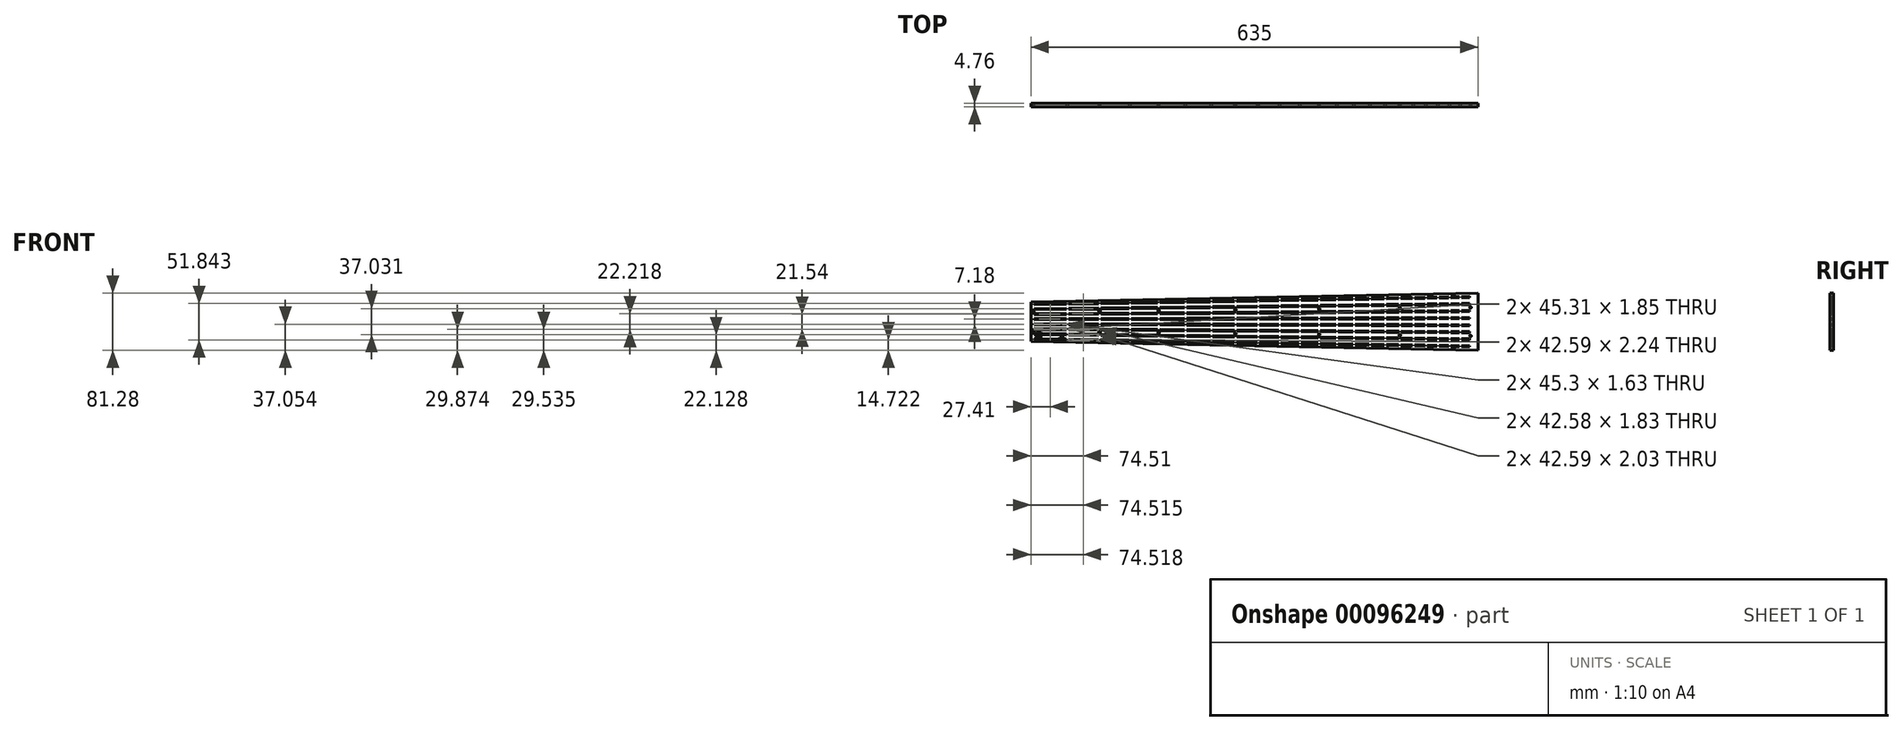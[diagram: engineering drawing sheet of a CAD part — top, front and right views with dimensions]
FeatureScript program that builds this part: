
annotation { "Feature Type Name" : "Feature", "Feature Type Description" : "" }
export const myFeature = defineFeature(function(context is Context, id is Id, definition is map)
    precondition{}
    {
        {
            var Q0;
            Q0=qCreatedBy(makeId("Front.planeOp"),FACE);
            var sketch = newSketch(context, id + "F0", { "sketchPlane" : qUnion([Q0])});
            skLineSegment(sketch, "E0", {"start": v(0, 3.52) * mm, "end": v(648.16, -7.37) * mm, "construction": true});
            skLineSegment(sketch, "E1", {"start": v(0, 4.29) * mm, "end": v(642.9, -6.52) * mm, "construction": true});
            skLineSegment(sketch, "E2", {"start": v(4.76, 3.44) * mm, "end": v(4.77, 4.2) * mm});
            skLineSegment(sketch, "E3", {"start": v(4.77, 4.2) * mm, "end": v(50.06, 3.45) * mm});
            skLineSegment(sketch, "E4", {"start": v(50.06, 3.45) * mm, "end": v(50.05, 2.68) * mm});
            skLineSegment(sketch, "E5", {"start": v(53.23, 2.63) * mm, "end": v(53.24, 3.4) * mm});
            skLineSegment(sketch, "E6", {"start": v(53.24, 3.4) * mm, "end": v(95.8, 2.68) * mm});
            skLineSegment(sketch, "E7", {"start": v(95.8, 2.68) * mm, "end": v(95.8, 1.91) * mm});
            skLineSegment(sketch, "E8", {"start": v(98.97, 1.86) * mm, "end": v(98.98, 2.62) * mm});
            skLineSegment(sketch, "E9", {"start": v(98.98, 2.62) * mm, "end": v(138.98, 1.95) * mm});
            skLineSegment(sketch, "E10", {"start": v(138.98, 1.95) * mm, "end": v(138.97, 1.19) * mm});
            skLineSegment(sketch, "E11", {"start": v(142.14, 1.14) * mm, "end": v(142.16, 1.9) * mm});
            skLineSegment(sketch, "E12", {"start": v(142.16, 1.9) * mm, "end": v(179.73, 1.27) * mm});
            skLineSegment(sketch, "E13", {"start": v(179.73, 1.27) * mm, "end": v(179.72, 0.5) * mm});
            skLineSegment(sketch, "E14", {"start": v(182.89, 0.45) * mm, "end": v(182.9, 1.21) * mm});
            skLineSegment(sketch, "E15", {"start": v(182.9, 1.21) * mm, "end": v(218.2, 0.62) * mm, "construction": true});
            skLineSegment(sketch, "E16", {"start": v(218.2, 0.62) * mm, "end": v(218.19, -0.14) * mm});
            skLineSegment(sketch, "E17", {"start": v(221.36, -0.2) * mm, "end": v(221.38, 0.57) * mm});
            skLineSegment(sketch, "E18", {"start": v(221.38, 0.57) * mm, "end": v(254.5, 0.01) * mm});
            skLineSegment(sketch, "E19", {"start": v(254.5, 0.01) * mm, "end": v(254.5, -0.75) * mm});
            skLineSegment(sketch, "E20", {"start": v(257.67, -0.8) * mm, "end": v(257.68, -0.04) * mm});
            skLineSegment(sketch, "E21", {"start": v(257.68, -0.04) * mm, "end": v(288.78, -0.57) * mm});
            skLineSegment(sketch, "E22", {"start": v(288.78, -0.57) * mm, "end": v(288.76, -1.33) * mm});
            skLineSegment(sketch, "E23", {"start": v(291.94, -1.38) * mm, "end": v(291.95, -0.62) * mm});
            skLineSegment(sketch, "E24", {"start": v(291.95, -0.62) * mm, "end": v(321.12, -1.1) * mm});
            skLineSegment(sketch, "E25", {"start": v(321.12, -1.1) * mm, "end": v(321.1, -1.87) * mm});
            skLineSegment(sketch, "E26", {"start": v(324.28, -1.92) * mm, "end": v(324.3, -1.16) * mm});
            skLineSegment(sketch, "E27", {"start": v(324.3, -1.16) * mm, "end": v(351.65, -1.62) * mm});
            skLineSegment(sketch, "E28", {"start": v(351.65, -1.62) * mm, "end": v(351.64, -2.38) * mm});
            skLineSegment(sketch, "E29", {"start": v(182.9, 1.21) * mm, "end": v(218.2, 0.62) * mm});
            skLineSegment(sketch, "E30", {"start": v(354.81, -2.44) * mm, "end": v(354.83, -1.68) * mm});
            skLineSegment(sketch, "E31", {"start": v(354.83, -1.68) * mm, "end": v(380.47, -2.1) * mm});
            skLineSegment(sketch, "E32", {"start": v(380.47, -2.1) * mm, "end": v(380.45, -2.87) * mm});
            skLineSegment(sketch, "E33", {"start": v(383.63, -2.92) * mm, "end": v(383.64, -2.16) * mm});
            skLineSegment(sketch, "E34", {"start": v(383.64, -2.16) * mm, "end": v(407.67, -2.56) * mm});
            skLineSegment(sketch, "E35", {"start": v(407.67, -2.56) * mm, "end": v(407.65, -3.33) * mm});
            skLineSegment(sketch, "E36", {"start": v(410.83, -3.38) * mm, "end": v(410.84, -2.62) * mm});
            skLineSegment(sketch, "E37", {"start": v(410.84, -2.62) * mm, "end": v(433.34, -3) * mm});
            skLineSegment(sketch, "E38", {"start": v(433.34, -3) * mm, "end": v(433.33, -3.76) * mm});
            skLineSegment(sketch, "E39", {"start": v(436.5, -3.8) * mm, "end": v(436.51, -3.05) * mm});
            skLineSegment(sketch, "E40", {"start": v(436.51, -3.05) * mm, "end": v(457.57, -3.4) * mm});
            skLineSegment(sketch, "E41", {"start": v(457.57, -3.4) * mm, "end": v(457.56, -4.16) * mm});
            skLineSegment(sketch, "E42", {"start": v(460.73, -4.22) * mm, "end": v(460.75, -3.46) * mm});
            skLineSegment(sketch, "E43", {"start": v(460.75, -3.46) * mm, "end": v(480.44, -3.79) * mm});
            skLineSegment(sketch, "E44", {"start": v(480.44, -3.79) * mm, "end": v(480.43, -4.55) * mm});
            skLineSegment(sketch, "E45", {"start": v(483.6, -4.6) * mm, "end": v(483.62, -3.84) * mm});
            skLineSegment(sketch, "E46", {"start": v(483.62, -3.84) * mm, "end": v(502.03, -4.15) * mm});
            skLineSegment(sketch, "E47", {"start": v(502.03, -4.15) * mm, "end": v(502.02, -4.91) * mm});
            skLineSegment(sketch, "E48", {"start": v(505.2, -4.96) * mm, "end": v(505.2, -4.2) * mm});
            skLineSegment(sketch, "E49", {"start": v(505.2, -4.2) * mm, "end": v(522.4, -4.5) * mm});
            skLineSegment(sketch, "E50", {"start": v(522.4, -4.5) * mm, "end": v(522.4, -5.25) * mm});
            skLineSegment(sketch, "E51", {"start": v(525.57, -5.3) * mm, "end": v(525.58, -4.54) * mm});
            skLineSegment(sketch, "E52", {"start": v(525.58, -4.54) * mm, "end": v(541.64, -4.81) * mm});
            skLineSegment(sketch, "E53", {"start": v(541.64, -4.81) * mm, "end": v(541.63, -5.58) * mm});
            skLineSegment(sketch, "E54", {"start": v(544.8, -5.63) * mm, "end": v(544.81, -4.87) * mm});
            skLineSegment(sketch, "E55", {"start": v(544.81, -4.87) * mm, "end": v(559.8, -5.12) * mm});
            skLineSegment(sketch, "E56", {"start": v(559.8, -5.12) * mm, "end": v(559.78, -5.88) * mm});
            skLineSegment(sketch, "E57", {"start": v(562.95, -5.93) * mm, "end": v(562.97, -5.17) * mm});
            skLineSegment(sketch, "E58", {"start": v(562.97, -5.17) * mm, "end": v(576.93, -5.4) * mm});
            skLineSegment(sketch, "E59", {"start": v(576.93, -5.4) * mm, "end": v(576.91, -6.17) * mm});
            skLineSegment(sketch, "E60", {"start": v(580.09, -6.22) * mm, "end": v(580.1, -5.46) * mm});
            skLineSegment(sketch, "E61", {"start": v(580.1, -5.46) * mm, "end": v(593.1, -5.68) * mm});
            skLineSegment(sketch, "E62", {"start": v(593.1, -5.68) * mm, "end": v(593.09, -6.44) * mm});
            skLineSegment(sketch, "E63", {"start": v(596.26, -6.5) * mm, "end": v(596.27, -5.73) * mm});
            skLineSegment(sketch, "E64", {"start": v(596.27, -5.73) * mm, "end": v(608.36, -5.94) * mm});
            skLineSegment(sketch, "E65", {"start": v(608.36, -5.94) * mm, "end": v(608.35, -6.7) * mm});
            skLineSegment(sketch, "E66", {"start": v(611.53, -6.75) * mm, "end": v(611.54, -5.99) * mm});
            skLineSegment(sketch, "E67", {"start": v(611.54, -5.99) * mm, "end": v(622.77, -6.18) * mm});
            skLineSegment(sketch, "E68", {"start": v(622.77, -6.18) * mm, "end": v(622.76, -6.94) * mm});
            skLineSegment(sketch, "E69.MirrorCS", {"start": v(182.89, 0.45) * mm, "end": v(182.88, -0.31) * mm});
            skLineSegment(sketch, "E70.MirrorCS", {"start": v(608.34, -7.46) * mm, "end": v(608.35, -6.7) * mm});
            skLineSegment(sketch, "E71.MirrorCS", {"start": v(221.36, -0.2) * mm, "end": v(221.35, -0.96) * mm});
            skLineSegment(sketch, "E72.MirrorCS", {"start": v(559.77, -6.64) * mm, "end": v(559.78, -5.88) * mm});
            skLineSegment(sketch, "E73.MirrorCS", {"start": v(218.18, -0.9) * mm, "end": v(218.19, -0.14) * mm});
            skLineSegment(sketch, "E74.MirrorCS", {"start": v(291.94, -1.38) * mm, "end": v(291.92, -2.14) * mm});
            skLineSegment(sketch, "E75.MirrorCS", {"start": v(95.78, 1.15) * mm, "end": v(95.8, 1.91) * mm});
            skLineSegment(sketch, "E76.MirrorCS", {"start": v(50.04, 1.92) * mm, "end": v(50.05, 2.68) * mm});
            skLineSegment(sketch, "E77.MirrorCS", {"start": v(611.53, -6.75) * mm, "end": v(611.51, -7.51) * mm});
            skLineSegment(sketch, "E78.MirrorCS", {"start": v(596.26, -6.5) * mm, "end": v(596.25, -7.26) * mm});
            skLineSegment(sketch, "E79.MirrorCS", {"start": v(324.28, -1.92) * mm, "end": v(324.27, -2.69) * mm});
            skLineSegment(sketch, "E80.MirrorCS", {"start": v(580.09, -6.22) * mm, "end": v(580.08, -6.98) * mm});
            skLineSegment(sketch, "E81.MirrorCS", {"start": v(480.42, -5.3) * mm, "end": v(480.43, -4.55) * mm});
            skLineSegment(sketch, "E82.MirrorCS", {"start": v(407.64, -4.09) * mm, "end": v(407.65, -3.33) * mm});
            skLineSegment(sketch, "E83.MirrorCS", {"start": v(593.07, -7.2) * mm, "end": v(593.09, -6.44) * mm});
            skLineSegment(sketch, "E84.MirrorCS", {"start": v(483.6, -4.6) * mm, "end": v(483.6, -5.36) * mm});
            skLineSegment(sketch, "E85.MirrorCS", {"start": v(580.08, -6.98) * mm, "end": v(593.07, -7.2) * mm});
            skLineSegment(sketch, "E86.MirrorCS", {"start": v(522.38, -6.01) * mm, "end": v(522.4, -5.25) * mm});
            skLineSegment(sketch, "E87.MirrorCS", {"start": v(321.1, -2.63) * mm, "end": v(321.1, -1.87) * mm});
            skLineSegment(sketch, "E88.MirrorCS", {"start": v(457.55, -4.93) * mm, "end": v(457.56, -4.16) * mm});
            skLineSegment(sketch, "E89.MirrorCS", {"start": v(562.95, -5.93) * mm, "end": v(562.94, -6.7) * mm});
            skLineSegment(sketch, "E90.MirrorCS", {"start": v(383.63, -2.92) * mm, "end": v(383.62, -3.68) * mm});
            skLineSegment(sketch, "E91.MirrorCS", {"start": v(380.44, -3.63) * mm, "end": v(380.45, -2.87) * mm});
            skLineSegment(sketch, "E92.MirrorCS", {"start": v(505.2, -4.96) * mm, "end": v(505.18, -5.73) * mm});
            skLineSegment(sketch, "E93.MirrorCS", {"start": v(596.25, -7.26) * mm, "end": v(608.34, -7.46) * mm});
            skLineSegment(sketch, "E94.MirrorCS", {"start": v(544.79, -6.4) * mm, "end": v(559.77, -6.64) * mm});
            skLineSegment(sketch, "E95.MirrorCS", {"start": v(142.14, 1.14) * mm, "end": v(142.13, 0.37) * mm});
            skLineSegment(sketch, "E96.MirrorCS", {"start": v(138.96, 0.43) * mm, "end": v(138.97, 1.19) * mm});
            skLineSegment(sketch, "E97.MirrorCS", {"start": v(98.97, 1.86) * mm, "end": v(98.96, 1.1) * mm});
            skLineSegment(sketch, "E98.MirrorCS", {"start": v(53.23, 2.63) * mm, "end": v(53.21, 1.87) * mm});
            skLineSegment(sketch, "E99.MirrorCS", {"start": v(4.76, 3.44) * mm, "end": v(4.75, 2.68) * mm});
            skLineSegment(sketch, "E100.MirrorCS", {"start": v(179.7, -0.26) * mm, "end": v(179.72, 0.5) * mm});
            skLineSegment(sketch, "E101.MirrorCS", {"start": v(433.31, -4.52) * mm, "end": v(433.33, -3.76) * mm});
            skLineSegment(sketch, "E102.MirrorCS", {"start": v(544.8, -5.63) * mm, "end": v(544.79, -6.4) * mm});
            skLineSegment(sketch, "E103.MirrorCS", {"start": v(502, -5.67) * mm, "end": v(502.02, -4.91) * mm});
            skLineSegment(sketch, "E104.MirrorCS", {"start": v(288.75, -2.09) * mm, "end": v(288.76, -1.33) * mm});
            skLineSegment(sketch, "E105.MirrorCS", {"start": v(562.94, -6.7) * mm, "end": v(576.9, -6.93) * mm});
            skLineSegment(sketch, "E106.MirrorCS", {"start": v(254.48, -1.51) * mm, "end": v(254.5, -0.75) * mm});
            skLineSegment(sketch, "E107.MirrorCS", {"start": v(611.51, -7.51) * mm, "end": v(622.75, -7.7) * mm});
            skLineSegment(sketch, "E108.MirrorCS", {"start": v(525.57, -5.3) * mm, "end": v(525.56, -6.07) * mm});
            skLineSegment(sketch, "E109.MirrorCS", {"start": v(351.63, -3.15) * mm, "end": v(351.64, -2.38) * mm});
            skLineSegment(sketch, "E110.MirrorCS", {"start": v(410.83, -3.38) * mm, "end": v(410.82, -4.14) * mm});
            skLineSegment(sketch, "E111.MirrorCS", {"start": v(576.9, -6.93) * mm, "end": v(576.91, -6.17) * mm});
            skLineSegment(sketch, "E112.MirrorCS", {"start": v(257.67, -0.8) * mm, "end": v(257.66, -1.57) * mm});
            skLineSegment(sketch, "E113.MirrorCS", {"start": v(622.75, -7.7) * mm, "end": v(622.76, -6.94) * mm});
            skLineSegment(sketch, "E114.MirrorCS", {"start": v(354.81, -2.44) * mm, "end": v(354.8, -3.2) * mm});
            skLineSegment(sketch, "E115.MirrorCS", {"start": v(505.18, -5.73) * mm, "end": v(522.38, -6.01) * mm});
            skLineSegment(sketch, "E116.MirrorCS", {"start": v(436.5, -3.8) * mm, "end": v(436.49, -4.57) * mm});
            skLineSegment(sketch, "E117.MirrorCS", {"start": v(182.88, -0.31) * mm, "end": v(218.18, -0.9) * mm, "construction": true});
            skLineSegment(sketch, "E118.MirrorCS", {"start": v(460.73, -4.22) * mm, "end": v(460.72, -4.98) * mm});
            skLineSegment(sketch, "E119.MirrorCS", {"start": v(541.61, -6.34) * mm, "end": v(541.63, -5.58) * mm});
            skLineSegment(sketch, "E120.MirrorCS", {"start": v(525.56, -6.07) * mm, "end": v(541.61, -6.34) * mm});
            skLineSegment(sketch, "E121.MirrorCS", {"start": v(221.35, -0.96) * mm, "end": v(254.48, -1.51) * mm});
            skLineSegment(sketch, "E122.MirrorCS", {"start": v(383.62, -3.68) * mm, "end": v(407.64, -4.09) * mm});
            skLineSegment(sketch, "E123.MirrorCS", {"start": v(291.92, -2.14) * mm, "end": v(321.1, -2.63) * mm});
            skLineSegment(sketch, "E124.MirrorCS", {"start": v(436.49, -4.57) * mm, "end": v(457.55, -4.93) * mm});
            skLineSegment(sketch, "E125.MirrorCS", {"start": v(142.13, 0.37) * mm, "end": v(179.7, -0.26) * mm});
            skLineSegment(sketch, "E126.MirrorCS", {"start": v(53.21, 1.87) * mm, "end": v(95.78, 1.15) * mm});
            skLineSegment(sketch, "E127.MirrorCS", {"start": v(4.75, 2.68) * mm, "end": v(50.04, 1.92) * mm});
            skLineSegment(sketch, "E128.MirrorCS", {"start": v(354.8, -3.2) * mm, "end": v(380.44, -3.63) * mm});
            skLineSegment(sketch, "E129.MirrorCS", {"start": v(257.66, -1.57) * mm, "end": v(288.75, -2.09) * mm});
            skLineSegment(sketch, "E130.MirrorCS", {"start": v(483.6, -5.36) * mm, "end": v(502, -5.67) * mm});
            skLineSegment(sketch, "E131.MirrorCS", {"start": v(410.82, -4.14) * mm, "end": v(433.31, -4.52) * mm});
            skLineSegment(sketch, "E132.MirrorCS", {"start": v(182.88, -0.31) * mm, "end": v(218.18, -0.9) * mm});
            skLineSegment(sketch, "E133.MirrorCS", {"start": v(460.72, -4.98) * mm, "end": v(480.42, -5.3) * mm});
            skLineSegment(sketch, "E134.MirrorCS", {"start": v(324.27, -2.69) * mm, "end": v(351.63, -3.15) * mm});
            skLineSegment(sketch, "E135.MirrorCS", {"start": v(98.96, 1.1) * mm, "end": v(138.96, 0.43) * mm});
            skLineSegment(sketch, "E136", {"start": v(-33.04, 0) * mm, "end": v(118.54, 0) * mm, "construction": true});
            skLineSegment(sketch, "E137", {"start": v(0, 10.57) * mm, "end": v(648.2, 2.8) * mm, "construction": true});
            skLineSegment(sketch, "E138", {"start": v(0, 11.33) * mm, "end": v(642.94, 3.62) * mm, "construction": true});
            skLineSegment(sketch, "E139", {"start": v(4.76, 10.52) * mm, "end": v(4.77, 11.28) * mm});
            skLineSegment(sketch, "E140", {"start": v(4.77, 11.28) * mm, "end": v(50.06, 10.73) * mm});
            skLineSegment(sketch, "E141", {"start": v(50.06, 10.73) * mm, "end": v(50.05, 9.97) * mm});
            skLineSegment(sketch, "E142", {"start": v(53.23, 9.93) * mm, "end": v(53.24, 10.7) * mm});
            skLineSegment(sketch, "E143", {"start": v(53.24, 10.7) * mm, "end": v(95.8, 10.19) * mm});
            skLineSegment(sketch, "E144", {"start": v(95.8, 10.19) * mm, "end": v(95.8, 9.42) * mm});
            skLineSegment(sketch, "E145", {"start": v(98.97, 9.38) * mm, "end": v(98.98, 10.15) * mm});
            skLineSegment(sketch, "E146", {"start": v(98.98, 10.15) * mm, "end": v(138.99, 9.67) * mm});
            skLineSegment(sketch, "E147", {"start": v(138.99, 9.67) * mm, "end": v(138.98, 8.9) * mm});
            skLineSegment(sketch, "E148", {"start": v(142.15, 8.87) * mm, "end": v(142.16, 9.63) * mm});
            skLineSegment(sketch, "E149", {"start": v(142.16, 9.63) * mm, "end": v(179.74, 9.18) * mm});
            skLineSegment(sketch, "E150", {"start": v(179.74, 9.18) * mm, "end": v(179.73, 8.42) * mm});
            skLineSegment(sketch, "E151", {"start": v(182.9, 8.38) * mm, "end": v(182.91, 9.14) * mm});
            skLineSegment(sketch, "E152", {"start": v(182.91, 9.14) * mm, "end": v(218.21, 8.72) * mm, "construction": true});
            skLineSegment(sketch, "E153", {"start": v(218.21, 8.72) * mm, "end": v(218.2, 7.95) * mm});
            skLineSegment(sketch, "E154", {"start": v(221.38, 7.92) * mm, "end": v(221.39, 8.68) * mm});
            skLineSegment(sketch, "E155", {"start": v(221.39, 8.68) * mm, "end": v(254.52, 8.28) * mm});
            skLineSegment(sketch, "E156", {"start": v(254.52, 8.28) * mm, "end": v(254.51, 7.52) * mm});
            skLineSegment(sketch, "E157", {"start": v(257.69, 7.48) * mm, "end": v(257.7, 8.24) * mm});
            skLineSegment(sketch, "E158", {"start": v(257.7, 8.24) * mm, "end": v(288.8, 7.87) * mm});
            skLineSegment(sketch, "E159", {"start": v(288.8, 7.87) * mm, "end": v(288.78, 7.1) * mm});
            skLineSegment(sketch, "E160", {"start": v(291.96, 7.07) * mm, "end": v(291.97, 7.83) * mm});
            skLineSegment(sketch, "E161", {"start": v(291.97, 7.83) * mm, "end": v(321.14, 7.48) * mm});
            skLineSegment(sketch, "E162", {"start": v(321.14, 7.48) * mm, "end": v(321.13, 6.72) * mm});
            skLineSegment(sketch, "E163", {"start": v(324.3, 6.68) * mm, "end": v(324.31, 7.44) * mm});
            skLineSegment(sketch, "E164", {"start": v(324.31, 7.44) * mm, "end": v(351.67, 7.11) * mm});
            skLineSegment(sketch, "E165", {"start": v(351.67, 7.11) * mm, "end": v(351.66, 6.35) * mm});
            skLineSegment(sketch, "E166", {"start": v(182.91, 9.14) * mm, "end": v(218.21, 8.72) * mm});
            skLineSegment(sketch, "E167", {"start": v(354.84, 6.31) * mm, "end": v(354.85, 7.08) * mm});
            skLineSegment(sketch, "E168", {"start": v(354.85, 7.08) * mm, "end": v(380.5, 6.77) * mm});
            skLineSegment(sketch, "E169", {"start": v(380.5, 6.77) * mm, "end": v(380.48, 6) * mm});
            skLineSegment(sketch, "E170", {"start": v(383.66, 5.97) * mm, "end": v(383.66, 6.73) * mm});
            skLineSegment(sketch, "E171", {"start": v(383.66, 6.73) * mm, "end": v(407.7, 6.44) * mm});
            skLineSegment(sketch, "E172", {"start": v(407.7, 6.44) * mm, "end": v(407.68, 5.68) * mm});
            skLineSegment(sketch, "E173", {"start": v(410.86, 5.64) * mm, "end": v(410.87, 6.4) * mm});
            skLineSegment(sketch, "E174", {"start": v(410.87, 6.4) * mm, "end": v(433.37, 6.13) * mm});
            skLineSegment(sketch, "E175", {"start": v(433.37, 6.13) * mm, "end": v(433.36, 5.37) * mm});
            skLineSegment(sketch, "E176", {"start": v(436.53, 5.33) * mm, "end": v(436.54, 6.1) * mm});
            skLineSegment(sketch, "E177", {"start": v(436.54, 6.1) * mm, "end": v(457.6, 5.84) * mm});
            skLineSegment(sketch, "E178", {"start": v(457.6, 5.84) * mm, "end": v(457.59, 5.08) * mm});
            skLineSegment(sketch, "E179", {"start": v(460.76, 5.04) * mm, "end": v(460.77, 5.8) * mm});
            skLineSegment(sketch, "E180", {"start": v(460.77, 5.8) * mm, "end": v(480.47, 5.57) * mm});
            skLineSegment(sketch, "E181", {"start": v(480.47, 5.57) * mm, "end": v(480.46, 4.8) * mm});
            skLineSegment(sketch, "E182", {"start": v(483.64, 4.77) * mm, "end": v(483.65, 5.53) * mm});
            skLineSegment(sketch, "E183", {"start": v(483.65, 5.53) * mm, "end": v(502.06, 5.3) * mm});
            skLineSegment(sketch, "E184", {"start": v(502.06, 5.3) * mm, "end": v(502.05, 4.55) * mm});
            skLineSegment(sketch, "E185", {"start": v(505.23, 4.5) * mm, "end": v(505.24, 5.27) * mm});
            skLineSegment(sketch, "E186", {"start": v(505.24, 5.27) * mm, "end": v(522.44, 5.07) * mm});
            skLineSegment(sketch, "E187", {"start": v(522.44, 5.07) * mm, "end": v(522.43, 4.3) * mm});
            skLineSegment(sketch, "E188", {"start": v(525.6, 4.27) * mm, "end": v(525.61, 5.03) * mm});
            skLineSegment(sketch, "E189", {"start": v(525.61, 5.03) * mm, "end": v(541.67, 4.83) * mm});
            skLineSegment(sketch, "E190", {"start": v(541.67, 4.83) * mm, "end": v(541.66, 4.07) * mm});
            skLineSegment(sketch, "E191", {"start": v(544.84, 4.03) * mm, "end": v(544.85, 4.8) * mm});
            skLineSegment(sketch, "E192", {"start": v(544.85, 4.8) * mm, "end": v(559.83, 4.62) * mm});
            skLineSegment(sketch, "E193", {"start": v(559.83, 4.62) * mm, "end": v(559.82, 3.85) * mm});
            skLineSegment(sketch, "E194", {"start": v(563, 3.82) * mm, "end": v(563, 4.58) * mm});
            skLineSegment(sketch, "E195", {"start": v(563, 4.58) * mm, "end": v(576.96, 4.41) * mm});
            skLineSegment(sketch, "E196", {"start": v(576.96, 4.41) * mm, "end": v(576.95, 3.65) * mm});
            skLineSegment(sketch, "E197", {"start": v(580.13, 3.61) * mm, "end": v(580.14, 4.37) * mm});
            skLineSegment(sketch, "E198", {"start": v(580.14, 4.37) * mm, "end": v(593.14, 4.22) * mm});
            skLineSegment(sketch, "E199", {"start": v(593.14, 4.22) * mm, "end": v(593.13, 3.45) * mm});
            skLineSegment(sketch, "E200", {"start": v(596.3, 3.42) * mm, "end": v(596.31, 4.18) * mm});
            skLineSegment(sketch, "E201", {"start": v(596.31, 4.18) * mm, "end": v(608.4, 4.03) * mm});
            skLineSegment(sketch, "E202", {"start": v(608.4, 4.03) * mm, "end": v(608.4, 3.27) * mm});
            skLineSegment(sketch, "E203", {"start": v(611.57, 3.23) * mm, "end": v(611.58, 4) * mm});
            skLineSegment(sketch, "E204", {"start": v(611.58, 4) * mm, "end": v(622.81, 3.86) * mm});
            skLineSegment(sketch, "E205", {"start": v(622.81, 3.86) * mm, "end": v(622.8, 3.1) * mm});
            skLineSegment(sketch, "E206.MirrorCS", {"start": v(182.9, 8.38) * mm, "end": v(182.9, 7.62) * mm});
            skLineSegment(sketch, "E207.MirrorCS", {"start": v(608.38, 2.5) * mm, "end": v(608.4, 3.27) * mm});
            skLineSegment(sketch, "E208.MirrorCS", {"start": v(221.38, 7.92) * mm, "end": v(221.37, 7.15) * mm});
            skLineSegment(sketch, "E209.MirrorCS", {"start": v(559.8, 3.1) * mm, "end": v(559.82, 3.85) * mm});
            skLineSegment(sketch, "E210.MirrorCS", {"start": v(218.2, 7.2) * mm, "end": v(218.2, 7.95) * mm});
            skLineSegment(sketch, "E211.MirrorCS", {"start": v(291.96, 7.07) * mm, "end": v(291.95, 6.3) * mm});
            skLineSegment(sketch, "E212.MirrorCS", {"start": v(95.8, 8.66) * mm, "end": v(95.8, 9.42) * mm});
            skLineSegment(sketch, "E213.MirrorCS", {"start": v(50.05, 9.21) * mm, "end": v(50.05, 9.97) * mm});
            skLineSegment(sketch, "E214.MirrorCS", {"start": v(611.57, 3.23) * mm, "end": v(611.56, 2.47) * mm});
            skLineSegment(sketch, "E215.MirrorCS", {"start": v(596.3, 3.42) * mm, "end": v(596.3, 2.65) * mm});
            skLineSegment(sketch, "E216.MirrorCS", {"start": v(324.3, 6.68) * mm, "end": v(324.3, 5.92) * mm});
            skLineSegment(sketch, "E217.MirrorCS", {"start": v(580.13, 3.61) * mm, "end": v(580.12, 2.85) * mm});
            skLineSegment(sketch, "E218.MirrorCS", {"start": v(480.45, 4.05) * mm, "end": v(480.46, 4.8) * mm});
            skLineSegment(sketch, "E219.MirrorCS", {"start": v(407.67, 4.92) * mm, "end": v(407.68, 5.68) * mm});
            skLineSegment(sketch, "E220.MirrorCS", {"start": v(593.12, 2.7) * mm, "end": v(593.13, 3.45) * mm});
            skLineSegment(sketch, "E221.MirrorCS", {"start": v(483.64, 4.77) * mm, "end": v(483.63, 4) * mm});
            skLineSegment(sketch, "E222.MirrorCS", {"start": v(580.12, 2.85) * mm, "end": v(593.12, 2.7) * mm});
            skLineSegment(sketch, "E223.MirrorCS", {"start": v(522.42, 3.54) * mm, "end": v(522.43, 4.3) * mm});
            skLineSegment(sketch, "E224.MirrorCS", {"start": v(321.12, 5.96) * mm, "end": v(321.13, 6.72) * mm});
            skLineSegment(sketch, "E225.MirrorCS", {"start": v(457.58, 4.32) * mm, "end": v(457.59, 5.08) * mm});
            skLineSegment(sketch, "E226.MirrorCS", {"start": v(563, 3.82) * mm, "end": v(562.98, 3.05) * mm});
            skLineSegment(sketch, "E227.MirrorCS", {"start": v(383.66, 5.97) * mm, "end": v(383.65, 5.2) * mm});
            skLineSegment(sketch, "E228.MirrorCS", {"start": v(380.47, 5.24) * mm, "end": v(380.48, 6) * mm});
            skLineSegment(sketch, "E229.MirrorCS", {"start": v(505.23, 4.5) * mm, "end": v(505.22, 3.75) * mm});
            skLineSegment(sketch, "E230.MirrorCS", {"start": v(596.3, 2.65) * mm, "end": v(608.38, 2.5) * mm});
            skLineSegment(sketch, "E231.MirrorCS", {"start": v(544.83, 3.27) * mm, "end": v(559.8, 3.1) * mm});
            skLineSegment(sketch, "E232.MirrorCS", {"start": v(142.15, 8.87) * mm, "end": v(142.15, 8.1) * mm});
            skLineSegment(sketch, "E233.MirrorCS", {"start": v(138.97, 8.14) * mm, "end": v(138.98, 8.9) * mm});
            skLineSegment(sketch, "E234.MirrorCS", {"start": v(98.97, 9.38) * mm, "end": v(98.97, 8.62) * mm});
            skLineSegment(sketch, "E235.MirrorCS", {"start": v(53.23, 9.93) * mm, "end": v(53.22, 9.17) * mm});
            skLineSegment(sketch, "E236.MirrorCS", {"start": v(4.76, 10.52) * mm, "end": v(4.75, 9.75) * mm});
            skLineSegment(sketch, "E237.MirrorCS", {"start": v(179.72, 7.65) * mm, "end": v(179.73, 8.42) * mm});
            skLineSegment(sketch, "E238.MirrorCS", {"start": v(433.35, 4.61) * mm, "end": v(433.36, 5.37) * mm});
            skLineSegment(sketch, "E239.MirrorCS", {"start": v(544.84, 4.03) * mm, "end": v(544.83, 3.27) * mm});
            skLineSegment(sketch, "E240.MirrorCS", {"start": v(502.04, 3.79) * mm, "end": v(502.05, 4.55) * mm});
            skLineSegment(sketch, "E241.MirrorCS", {"start": v(288.77, 6.35) * mm, "end": v(288.78, 7.1) * mm});
            skLineSegment(sketch, "E242.MirrorCS", {"start": v(562.98, 3.05) * mm, "end": v(576.94, 2.89) * mm});
            skLineSegment(sketch, "E243.MirrorCS", {"start": v(254.5, 6.76) * mm, "end": v(254.51, 7.52) * mm});
            skLineSegment(sketch, "E244.MirrorCS", {"start": v(611.56, 2.47) * mm, "end": v(622.8, 2.34) * mm});
            skLineSegment(sketch, "E245.MirrorCS", {"start": v(525.6, 4.27) * mm, "end": v(525.6, 3.5) * mm});
            skLineSegment(sketch, "E246.MirrorCS", {"start": v(351.65, 5.6) * mm, "end": v(351.66, 6.35) * mm});
            skLineSegment(sketch, "E247.MirrorCS", {"start": v(410.86, 5.64) * mm, "end": v(410.85, 4.88) * mm});
            skLineSegment(sketch, "E248.MirrorCS", {"start": v(576.94, 2.89) * mm, "end": v(576.95, 3.65) * mm});
            skLineSegment(sketch, "E249.MirrorCS", {"start": v(257.69, 7.48) * mm, "end": v(257.68, 6.72) * mm});
            skLineSegment(sketch, "E250.MirrorCS", {"start": v(622.8, 2.34) * mm, "end": v(622.8, 3.1) * mm});
            skLineSegment(sketch, "E251.MirrorCS", {"start": v(354.84, 6.31) * mm, "end": v(354.83, 5.55) * mm});
            skLineSegment(sketch, "E252.MirrorCS", {"start": v(505.22, 3.75) * mm, "end": v(522.42, 3.54) * mm});
            skLineSegment(sketch, "E253.MirrorCS", {"start": v(436.53, 5.33) * mm, "end": v(436.52, 4.57) * mm});
            skLineSegment(sketch, "E254.MirrorCS", {"start": v(182.9, 7.62) * mm, "end": v(218.2, 7.2) * mm, "construction": true});
            skLineSegment(sketch, "E255.MirrorCS", {"start": v(460.76, 5.04) * mm, "end": v(460.76, 4.28) * mm});
            skLineSegment(sketch, "E256.MirrorCS", {"start": v(541.65, 3.31) * mm, "end": v(541.66, 4.07) * mm});
            skLineSegment(sketch, "E257.MirrorCS", {"start": v(525.6, 3.5) * mm, "end": v(541.65, 3.31) * mm});
            skLineSegment(sketch, "E258.MirrorCS", {"start": v(221.37, 7.15) * mm, "end": v(254.5, 6.76) * mm});
            skLineSegment(sketch, "E259.MirrorCS", {"start": v(383.65, 5.2) * mm, "end": v(407.67, 4.92) * mm});
            skLineSegment(sketch, "E260.MirrorCS", {"start": v(291.95, 6.3) * mm, "end": v(321.12, 5.96) * mm});
            skLineSegment(sketch, "E261.MirrorCS", {"start": v(436.52, 4.57) * mm, "end": v(457.58, 4.32) * mm});
            skLineSegment(sketch, "E262.MirrorCS", {"start": v(142.15, 8.1) * mm, "end": v(179.72, 7.65) * mm});
            skLineSegment(sketch, "E263.MirrorCS", {"start": v(53.22, 9.17) * mm, "end": v(95.8, 8.66) * mm});
            skLineSegment(sketch, "E264.MirrorCS", {"start": v(4.75, 9.75) * mm, "end": v(50.05, 9.21) * mm});
            skLineSegment(sketch, "E265.MirrorCS", {"start": v(354.83, 5.55) * mm, "end": v(380.47, 5.24) * mm});
            skLineSegment(sketch, "E266.MirrorCS", {"start": v(257.68, 6.72) * mm, "end": v(288.77, 6.35) * mm});
            skLineSegment(sketch, "E267.MirrorCS", {"start": v(483.63, 4) * mm, "end": v(502.04, 3.79) * mm});
            skLineSegment(sketch, "E268.MirrorCS", {"start": v(410.85, 4.88) * mm, "end": v(433.35, 4.61) * mm});
            skLineSegment(sketch, "E269.MirrorCS", {"start": v(182.9, 7.62) * mm, "end": v(218.2, 7.2) * mm});
            skLineSegment(sketch, "E270.MirrorCS", {"start": v(460.76, 4.28) * mm, "end": v(480.45, 4.05) * mm});
            skLineSegment(sketch, "E271.MirrorCS", {"start": v(324.3, 5.92) * mm, "end": v(351.65, 5.6) * mm});
            skLineSegment(sketch, "E272.MirrorCS", {"start": v(98.97, 8.62) * mm, "end": v(138.97, 8.14) * mm});
            skLineSegment(sketch, "E273", {"start": v(0, 17.62) * mm, "end": v(648.23, 12.95) * mm, "construction": true});
            skLineSegment(sketch, "E274", {"start": v(0, 18.38) * mm, "end": v(642.97, 13.75) * mm, "construction": true});
            skLineSegment(sketch, "E275", {"start": v(4.76, 17.59) * mm, "end": v(4.77, 18.35) * mm});
            skLineSegment(sketch, "E276", {"start": v(4.77, 18.35) * mm, "end": v(50.06, 18.02) * mm});
            skLineSegment(sketch, "E277", {"start": v(50.06, 18.02) * mm, "end": v(50.06, 17.26) * mm});
            skLineSegment(sketch, "E278", {"start": v(53.23, 17.24) * mm, "end": v(53.24, 18) * mm});
            skLineSegment(sketch, "E279", {"start": v(53.24, 18) * mm, "end": v(95.81, 17.7) * mm});
            skLineSegment(sketch, "E280", {"start": v(95.81, 17.7) * mm, "end": v(95.8, 16.93) * mm});
            skLineSegment(sketch, "E281", {"start": v(98.98, 16.9) * mm, "end": v(98.99, 17.67) * mm});
            skLineSegment(sketch, "E282", {"start": v(98.99, 17.67) * mm, "end": v(139, 17.38) * mm});
            skLineSegment(sketch, "E283", {"start": v(139, 17.38) * mm, "end": v(138.99, 16.62) * mm});
            skLineSegment(sketch, "E284", {"start": v(142.16, 16.6) * mm, "end": v(142.17, 17.36) * mm});
            skLineSegment(sketch, "E285", {"start": v(142.17, 17.36) * mm, "end": v(179.74, 17.09) * mm});
            skLineSegment(sketch, "E286", {"start": v(179.74, 17.09) * mm, "end": v(179.74, 16.33) * mm});
            skLineSegment(sketch, "E287", {"start": v(182.91, 16.3) * mm, "end": v(182.92, 17.07) * mm});
            skLineSegment(sketch, "E288", {"start": v(182.92, 17.07) * mm, "end": v(218.22, 16.81) * mm, "construction": true});
            skLineSegment(sketch, "E289", {"start": v(218.22, 16.81) * mm, "end": v(218.21, 16.05) * mm});
            skLineSegment(sketch, "E290", {"start": v(221.39, 16.03) * mm, "end": v(221.4, 16.79) * mm});
            skLineSegment(sketch, "E291", {"start": v(221.4, 16.79) * mm, "end": v(254.53, 16.55) * mm});
            skLineSegment(sketch, "E292", {"start": v(254.53, 16.55) * mm, "end": v(254.52, 15.79) * mm});
            skLineSegment(sketch, "E293", {"start": v(257.7, 15.77) * mm, "end": v(257.7, 16.53) * mm});
            skLineSegment(sketch, "E294", {"start": v(257.7, 16.53) * mm, "end": v(288.8, 16.3) * mm});
            skLineSegment(sketch, "E295", {"start": v(288.8, 16.3) * mm, "end": v(288.8, 15.54) * mm});
            skLineSegment(sketch, "E296", {"start": v(291.97, 15.52) * mm, "end": v(291.98, 16.28) * mm});
            skLineSegment(sketch, "E297", {"start": v(291.98, 16.28) * mm, "end": v(321.15, 16.07) * mm});
            skLineSegment(sketch, "E298", {"start": v(321.15, 16.07) * mm, "end": v(321.14, 15.3) * mm});
            skLineSegment(sketch, "E299", {"start": v(324.32, 15.29) * mm, "end": v(324.33, 16.05) * mm});
            skLineSegment(sketch, "E300", {"start": v(324.33, 16.05) * mm, "end": v(351.68, 15.85) * mm});
            skLineSegment(sketch, "E301", {"start": v(351.68, 15.85) * mm, "end": v(351.68, 15.09) * mm});
            skLineSegment(sketch, "E302", {"start": v(182.92, 17.07) * mm, "end": v(218.22, 16.81) * mm});
            skLineSegment(sketch, "E303", {"start": v(354.85, 15.07) * mm, "end": v(354.86, 15.83) * mm});
            skLineSegment(sketch, "E304", {"start": v(354.86, 15.83) * mm, "end": v(380.5, 15.64) * mm});
            skLineSegment(sketch, "E305", {"start": v(380.5, 15.64) * mm, "end": v(380.5, 14.88) * mm});
            skLineSegment(sketch, "E306", {"start": v(383.67, 14.86) * mm, "end": v(383.68, 15.62) * mm});
            skLineSegment(sketch, "E307", {"start": v(383.68, 15.62) * mm, "end": v(407.7, 15.45) * mm});
            skLineSegment(sketch, "E308", {"start": v(407.7, 15.45) * mm, "end": v(407.7, 14.69) * mm});
            skLineSegment(sketch, "E309", {"start": v(410.88, 14.66) * mm, "end": v(410.88, 15.42) * mm});
            skLineSegment(sketch, "E310", {"start": v(410.88, 15.42) * mm, "end": v(433.38, 15.26) * mm});
            skLineSegment(sketch, "E311", {"start": v(433.38, 15.26) * mm, "end": v(433.38, 14.5) * mm});
            skLineSegment(sketch, "E312", {"start": v(436.55, 14.48) * mm, "end": v(436.56, 15.24) * mm});
            skLineSegment(sketch, "E313", {"start": v(436.56, 15.24) * mm, "end": v(457.62, 15.09) * mm});
            skLineSegment(sketch, "E314", {"start": v(457.62, 15.09) * mm, "end": v(457.61, 14.33) * mm});
            skLineSegment(sketch, "E315", {"start": v(460.79, 14.3) * mm, "end": v(460.8, 15.07) * mm});
            skLineSegment(sketch, "E316", {"start": v(460.8, 15.07) * mm, "end": v(480.5, 14.92) * mm});
            skLineSegment(sketch, "E317", {"start": v(480.5, 14.92) * mm, "end": v(480.49, 14.16) * mm});
            skLineSegment(sketch, "E318", {"start": v(483.66, 14.14) * mm, "end": v(483.67, 14.9) * mm});
            skLineSegment(sketch, "E319", {"start": v(483.67, 14.9) * mm, "end": v(502.08, 14.77) * mm});
            skLineSegment(sketch, "E320", {"start": v(502.08, 14.77) * mm, "end": v(502.08, 14) * mm});
            skLineSegment(sketch, "E321", {"start": v(505.25, 13.98) * mm, "end": v(505.26, 14.75) * mm});
            skLineSegment(sketch, "E322", {"start": v(505.26, 14.75) * mm, "end": v(522.46, 14.62) * mm});
            skLineSegment(sketch, "E323", {"start": v(522.46, 14.62) * mm, "end": v(522.45, 13.86) * mm});
            skLineSegment(sketch, "E324", {"start": v(525.63, 13.84) * mm, "end": v(525.63, 14.6) * mm});
            skLineSegment(sketch, "E325", {"start": v(525.63, 14.6) * mm, "end": v(541.7, 14.48) * mm});
            skLineSegment(sketch, "E326", {"start": v(541.7, 14.48) * mm, "end": v(541.69, 13.72) * mm});
            skLineSegment(sketch, "E327", {"start": v(544.86, 13.7) * mm, "end": v(544.87, 14.46) * mm});
            skLineSegment(sketch, "E328", {"start": v(544.87, 14.46) * mm, "end": v(559.85, 14.35) * mm});
            skLineSegment(sketch, "E329", {"start": v(559.85, 14.35) * mm, "end": v(559.84, 13.6) * mm});
            skLineSegment(sketch, "E330", {"start": v(563.02, 13.57) * mm, "end": v(563.03, 14.33) * mm});
            skLineSegment(sketch, "E331", {"start": v(563.03, 14.33) * mm, "end": v(576.99, 14.23) * mm});
            skLineSegment(sketch, "E332", {"start": v(576.99, 14.23) * mm, "end": v(576.98, 13.47) * mm});
            skLineSegment(sketch, "E333", {"start": v(580.16, 13.44) * mm, "end": v(580.16, 14.2) * mm});
            skLineSegment(sketch, "E334", {"start": v(580.16, 14.2) * mm, "end": v(593.16, 14.11) * mm});
            skLineSegment(sketch, "E335", {"start": v(593.16, 14.11) * mm, "end": v(593.16, 13.35) * mm});
            skLineSegment(sketch, "E336", {"start": v(596.33, 13.33) * mm, "end": v(596.34, 14.09) * mm});
            skLineSegment(sketch, "E337", {"start": v(596.34, 14.09) * mm, "end": v(608.43, 14) * mm});
            skLineSegment(sketch, "E338", {"start": v(608.43, 14) * mm, "end": v(608.42, 13.24) * mm});
            skLineSegment(sketch, "E339", {"start": v(611.6, 13.22) * mm, "end": v(611.6, 13.98) * mm});
            skLineSegment(sketch, "E340", {"start": v(611.6, 13.98) * mm, "end": v(622.84, 13.9) * mm});
            skLineSegment(sketch, "E341", {"start": v(622.84, 13.9) * mm, "end": v(622.83, 13.14) * mm});
            skLineSegment(sketch, "E342.MirrorCS", {"start": v(182.91, 16.3) * mm, "end": v(182.9, 15.54) * mm});
            skLineSegment(sketch, "E343.MirrorCS", {"start": v(608.42, 12.48) * mm, "end": v(608.42, 13.24) * mm});
            skLineSegment(sketch, "E344.MirrorCS", {"start": v(221.39, 16.03) * mm, "end": v(221.38, 15.27) * mm});
            skLineSegment(sketch, "E345.MirrorCS", {"start": v(559.84, 12.83) * mm, "end": v(559.84, 13.6) * mm});
            skLineSegment(sketch, "E346.MirrorCS", {"start": v(218.2, 15.29) * mm, "end": v(218.21, 16.05) * mm});
            skLineSegment(sketch, "E347.MirrorCS", {"start": v(291.97, 15.52) * mm, "end": v(291.97, 14.76) * mm});
            skLineSegment(sketch, "E348.MirrorCS", {"start": v(95.8, 16.17) * mm, "end": v(95.8, 16.93) * mm});
            skLineSegment(sketch, "E349.MirrorCS", {"start": v(50.05, 16.5) * mm, "end": v(50.06, 17.26) * mm});
            skLineSegment(sketch, "E350.MirrorCS", {"start": v(611.6, 13.22) * mm, "end": v(611.6, 12.46) * mm});
            skLineSegment(sketch, "E351.MirrorCS", {"start": v(596.33, 13.33) * mm, "end": v(596.32, 12.57) * mm});
            skLineSegment(sketch, "E352.MirrorCS", {"start": v(324.32, 15.29) * mm, "end": v(324.31, 14.52) * mm});
            skLineSegment(sketch, "E353.MirrorCS", {"start": v(580.16, 13.44) * mm, "end": v(580.15, 12.68) * mm});
            skLineSegment(sketch, "E354.MirrorCS", {"start": v(480.48, 13.4) * mm, "end": v(480.49, 14.16) * mm});
            skLineSegment(sketch, "E355.MirrorCS", {"start": v(407.7, 13.92) * mm, "end": v(407.7, 14.69) * mm});
            skLineSegment(sketch, "E356.MirrorCS", {"start": v(593.15, 12.59) * mm, "end": v(593.16, 13.35) * mm});
            skLineSegment(sketch, "E357.MirrorCS", {"start": v(483.66, 14.14) * mm, "end": v(483.65, 13.38) * mm});
            skLineSegment(sketch, "E358.MirrorCS", {"start": v(580.15, 12.68) * mm, "end": v(593.15, 12.59) * mm});
            skLineSegment(sketch, "E359.MirrorCS", {"start": v(522.45, 13.1) * mm, "end": v(522.45, 13.86) * mm});
            skLineSegment(sketch, "E360.MirrorCS", {"start": v(321.14, 14.55) * mm, "end": v(321.14, 15.3) * mm});
            skLineSegment(sketch, "E361.MirrorCS", {"start": v(457.6, 13.56) * mm, "end": v(457.61, 14.33) * mm});
            skLineSegment(sketch, "E362.MirrorCS", {"start": v(563.02, 13.57) * mm, "end": v(563.01, 12.8) * mm});
            skLineSegment(sketch, "E363.MirrorCS", {"start": v(383.67, 14.86) * mm, "end": v(383.67, 14.1) * mm});
            skLineSegment(sketch, "E364.MirrorCS", {"start": v(380.5, 14.12) * mm, "end": v(380.5, 14.88) * mm});
            skLineSegment(sketch, "E365.MirrorCS", {"start": v(505.25, 13.98) * mm, "end": v(505.25, 13.22) * mm});
            skLineSegment(sketch, "E366.MirrorCS", {"start": v(596.32, 12.57) * mm, "end": v(608.42, 12.48) * mm});
            skLineSegment(sketch, "E367.MirrorCS", {"start": v(544.86, 12.94) * mm, "end": v(559.84, 12.83) * mm});
            skLineSegment(sketch, "E368.MirrorCS", {"start": v(142.16, 16.6) * mm, "end": v(142.16, 15.84) * mm});
            skLineSegment(sketch, "E369.MirrorCS", {"start": v(138.98, 15.86) * mm, "end": v(138.99, 16.62) * mm});
            skLineSegment(sketch, "E370.MirrorCS", {"start": v(98.98, 16.9) * mm, "end": v(98.97, 16.15) * mm});
            skLineSegment(sketch, "E371.MirrorCS", {"start": v(53.23, 17.24) * mm, "end": v(53.23, 16.48) * mm});
            skLineSegment(sketch, "E372.MirrorCS", {"start": v(4.76, 17.59) * mm, "end": v(4.76, 16.82) * mm});
            skLineSegment(sketch, "E373.MirrorCS", {"start": v(179.73, 15.57) * mm, "end": v(179.74, 16.33) * mm});
            skLineSegment(sketch, "E374.MirrorCS", {"start": v(433.37, 13.74) * mm, "end": v(433.38, 14.5) * mm});
            skLineSegment(sketch, "E375.MirrorCS", {"start": v(544.86, 13.7) * mm, "end": v(544.86, 12.94) * mm});
            skLineSegment(sketch, "E376.MirrorCS", {"start": v(502.07, 13.24) * mm, "end": v(502.08, 14) * mm});
            skLineSegment(sketch, "E377.MirrorCS", {"start": v(288.8, 14.78) * mm, "end": v(288.8, 15.54) * mm});
            skLineSegment(sketch, "E378.MirrorCS", {"start": v(563.01, 12.8) * mm, "end": v(576.98, 12.7) * mm});
            skLineSegment(sketch, "E379.MirrorCS", {"start": v(254.52, 15.03) * mm, "end": v(254.52, 15.79) * mm});
            skLineSegment(sketch, "E380.MirrorCS", {"start": v(611.6, 12.46) * mm, "end": v(622.83, 12.37) * mm});
            skLineSegment(sketch, "E381.MirrorCS", {"start": v(525.63, 13.84) * mm, "end": v(525.62, 13.07) * mm});
            skLineSegment(sketch, "E382.MirrorCS", {"start": v(351.67, 14.33) * mm, "end": v(351.68, 15.09) * mm});
            skLineSegment(sketch, "E383.MirrorCS", {"start": v(410.88, 14.66) * mm, "end": v(410.87, 13.9) * mm});
            skLineSegment(sketch, "E384.MirrorCS", {"start": v(576.98, 12.7) * mm, "end": v(576.98, 13.47) * mm});
            skLineSegment(sketch, "E385.MirrorCS", {"start": v(257.7, 15.77) * mm, "end": v(257.7, 15) * mm});
            skLineSegment(sketch, "E386.MirrorCS", {"start": v(622.83, 12.37) * mm, "end": v(622.83, 13.14) * mm});
            skLineSegment(sketch, "E387.MirrorCS", {"start": v(354.85, 15.07) * mm, "end": v(354.85, 14.3) * mm});
            skLineSegment(sketch, "E388.MirrorCS", {"start": v(505.25, 13.22) * mm, "end": v(522.45, 13.1) * mm});
            skLineSegment(sketch, "E389.MirrorCS", {"start": v(436.55, 14.48) * mm, "end": v(436.55, 13.72) * mm});
            skLineSegment(sketch, "E390.MirrorCS", {"start": v(182.9, 15.54) * mm, "end": v(218.2, 15.29) * mm, "construction": true});
            skLineSegment(sketch, "E391.MirrorCS", {"start": v(460.79, 14.3) * mm, "end": v(460.78, 13.54) * mm});
            skLineSegment(sketch, "E392.MirrorCS", {"start": v(541.68, 12.96) * mm, "end": v(541.69, 13.72) * mm});
            skLineSegment(sketch, "E393.MirrorCS", {"start": v(525.62, 13.07) * mm, "end": v(541.68, 12.96) * mm});
            skLineSegment(sketch, "E394.MirrorCS", {"start": v(221.38, 15.27) * mm, "end": v(254.52, 15.03) * mm});
            skLineSegment(sketch, "E395.MirrorCS", {"start": v(383.67, 14.1) * mm, "end": v(407.7, 13.92) * mm});
            skLineSegment(sketch, "E396.MirrorCS", {"start": v(291.97, 14.76) * mm, "end": v(321.14, 14.55) * mm});
            skLineSegment(sketch, "E397.MirrorCS", {"start": v(436.55, 13.72) * mm, "end": v(457.6, 13.56) * mm});
            skLineSegment(sketch, "E398.MirrorCS", {"start": v(142.16, 15.84) * mm, "end": v(179.73, 15.57) * mm});
            skLineSegment(sketch, "E399.MirrorCS", {"start": v(53.23, 16.48) * mm, "end": v(95.8, 16.17) * mm});
            skLineSegment(sketch, "E400.MirrorCS", {"start": v(4.76, 16.82) * mm, "end": v(50.05, 16.5) * mm});
            skLineSegment(sketch, "E401.MirrorCS", {"start": v(354.85, 14.3) * mm, "end": v(380.5, 14.12) * mm});
            skLineSegment(sketch, "E402.MirrorCS", {"start": v(257.7, 15) * mm, "end": v(288.8, 14.78) * mm});
            skLineSegment(sketch, "E403.MirrorCS", {"start": v(483.65, 13.38) * mm, "end": v(502.07, 13.24) * mm});
            skLineSegment(sketch, "E404.MirrorCS", {"start": v(410.87, 13.9) * mm, "end": v(433.37, 13.74) * mm});
            skLineSegment(sketch, "E405.MirrorCS", {"start": v(182.9, 15.54) * mm, "end": v(218.2, 15.29) * mm});
            skLineSegment(sketch, "E406.MirrorCS", {"start": v(460.78, 13.54) * mm, "end": v(480.48, 13.4) * mm});
            skLineSegment(sketch, "E407.MirrorCS", {"start": v(324.31, 14.52) * mm, "end": v(351.67, 14.33) * mm});
            skLineSegment(sketch, "E408.MirrorCS", {"start": v(98.97, 16.15) * mm, "end": v(138.98, 15.86) * mm});
            skLineSegment(sketch, "E409", {"start": v(0, 24.67) * mm, "end": v(648.25, 23.11) * mm, "construction": true});
            skLineSegment(sketch, "E410", {"start": v(0, 25.43) * mm, "end": v(642.98, 23.89) * mm, "construction": true});
            skLineSegment(sketch, "E411", {"start": v(4.76, 24.66) * mm, "end": v(4.76, 25.42) * mm});
            skLineSegment(sketch, "E412", {"start": v(4.76, 25.42) * mm, "end": v(50.06, 25.31) * mm});
            skLineSegment(sketch, "E413", {"start": v(50.06, 25.31) * mm, "end": v(50.06, 24.55) * mm});
            skLineSegment(sketch, "E414", {"start": v(53.23, 24.54) * mm, "end": v(53.23, 25.3) * mm});
            skLineSegment(sketch, "E415", {"start": v(53.23, 25.3) * mm, "end": v(95.8, 25.2) * mm});
            skLineSegment(sketch, "E416", {"start": v(95.8, 25.2) * mm, "end": v(95.8, 24.44) * mm});
            skLineSegment(sketch, "E417", {"start": v(98.98, 24.43) * mm, "end": v(98.98, 25.2) * mm});
            skLineSegment(sketch, "E418", {"start": v(98.98, 25.2) * mm, "end": v(139, 25.1) * mm});
            skLineSegment(sketch, "E419", {"start": v(139, 25.1) * mm, "end": v(138.99, 24.34) * mm});
            skLineSegment(sketch, "E420", {"start": v(142.16, 24.33) * mm, "end": v(142.17, 25.1) * mm});
            skLineSegment(sketch, "E421", {"start": v(142.17, 25.1) * mm, "end": v(179.74, 25) * mm});
            skLineSegment(sketch, "E422", {"start": v(179.74, 25) * mm, "end": v(179.74, 24.24) * mm});
            skLineSegment(sketch, "E423", {"start": v(182.91, 24.23) * mm, "end": v(182.92, 25) * mm});
            skLineSegment(sketch, "E424", {"start": v(182.92, 25) * mm, "end": v(218.22, 24.9) * mm, "construction": true});
            skLineSegment(sketch, "E425", {"start": v(218.22, 24.9) * mm, "end": v(218.22, 24.15) * mm});
            skLineSegment(sketch, "E426", {"start": v(221.4, 24.14) * mm, "end": v(221.4, 24.9) * mm});
            skLineSegment(sketch, "E427", {"start": v(221.4, 24.9) * mm, "end": v(254.53, 24.82) * mm});
            skLineSegment(sketch, "E428", {"start": v(254.53, 24.82) * mm, "end": v(254.53, 24.06) * mm});
            skLineSegment(sketch, "E429", {"start": v(257.7, 24.05) * mm, "end": v(257.7, 24.81) * mm});
            skLineSegment(sketch, "E430", {"start": v(257.7, 24.81) * mm, "end": v(288.8, 24.74) * mm});
            skLineSegment(sketch, "E431", {"start": v(288.8, 24.74) * mm, "end": v(288.8, 23.98) * mm});
            skLineSegment(sketch, "E432", {"start": v(291.98, 23.97) * mm, "end": v(291.98, 24.73) * mm});
            skLineSegment(sketch, "E433", {"start": v(291.98, 24.73) * mm, "end": v(321.15, 24.66) * mm});
            skLineSegment(sketch, "E434", {"start": v(321.15, 24.66) * mm, "end": v(321.15, 23.9) * mm});
            skLineSegment(sketch, "E435", {"start": v(324.33, 23.9) * mm, "end": v(324.33, 24.65) * mm});
            skLineSegment(sketch, "E436", {"start": v(324.33, 24.65) * mm, "end": v(351.69, 24.59) * mm});
            skLineSegment(sketch, "E437", {"start": v(351.69, 24.59) * mm, "end": v(351.69, 23.83) * mm});
            skLineSegment(sketch, "E438", {"start": v(182.92, 25) * mm, "end": v(218.22, 24.9) * mm});
            skLineSegment(sketch, "E439", {"start": v(354.86, 23.82) * mm, "end": v(354.86, 24.58) * mm});
            skLineSegment(sketch, "E440", {"start": v(354.86, 24.58) * mm, "end": v(380.5, 24.52) * mm});
            skLineSegment(sketch, "E441", {"start": v(380.5, 24.52) * mm, "end": v(380.5, 23.76) * mm});
            skLineSegment(sketch, "E442", {"start": v(383.68, 23.75) * mm, "end": v(383.68, 24.51) * mm});
            skLineSegment(sketch, "E443", {"start": v(383.68, 24.51) * mm, "end": v(407.71, 24.45) * mm});
            skLineSegment(sketch, "E444", {"start": v(407.71, 24.45) * mm, "end": v(407.7, 23.7) * mm});
            skLineSegment(sketch, "E445", {"start": v(410.88, 23.68) * mm, "end": v(410.89, 24.45) * mm});
            skLineSegment(sketch, "E446", {"start": v(410.89, 24.45) * mm, "end": v(433.39, 24.4) * mm});
            skLineSegment(sketch, "E447", {"start": v(433.39, 24.4) * mm, "end": v(433.39, 23.63) * mm});
            skLineSegment(sketch, "E448", {"start": v(436.56, 23.62) * mm, "end": v(436.56, 24.38) * mm});
            skLineSegment(sketch, "E449", {"start": v(436.56, 24.38) * mm, "end": v(457.62, 24.33) * mm});
            skLineSegment(sketch, "E450", {"start": v(457.62, 24.33) * mm, "end": v(457.62, 23.57) * mm});
            skLineSegment(sketch, "E451", {"start": v(460.8, 23.56) * mm, "end": v(460.8, 24.33) * mm});
            skLineSegment(sketch, "E452", {"start": v(460.8, 24.33) * mm, "end": v(480.5, 24.28) * mm});
            skLineSegment(sketch, "E453", {"start": v(480.5, 24.28) * mm, "end": v(480.5, 23.52) * mm});
            skLineSegment(sketch, "E454", {"start": v(483.67, 23.5) * mm, "end": v(483.67, 24.27) * mm});
            skLineSegment(sketch, "E455", {"start": v(483.67, 24.27) * mm, "end": v(502.09, 24.23) * mm});
            skLineSegment(sketch, "E456", {"start": v(502.09, 24.23) * mm, "end": v(502.09, 23.46) * mm});
            skLineSegment(sketch, "E457", {"start": v(505.26, 23.46) * mm, "end": v(505.26, 24.22) * mm});
            skLineSegment(sketch, "E458", {"start": v(505.26, 24.22) * mm, "end": v(522.47, 24.18) * mm});
            skLineSegment(sketch, "E459", {"start": v(522.47, 24.18) * mm, "end": v(522.47, 23.42) * mm});
            skLineSegment(sketch, "E460", {"start": v(525.64, 23.4) * mm, "end": v(525.64, 24.17) * mm});
            skLineSegment(sketch, "E461", {"start": v(525.64, 24.17) * mm, "end": v(541.7, 24.13) * mm});
            skLineSegment(sketch, "E462", {"start": v(541.7, 24.13) * mm, "end": v(541.7, 23.37) * mm});
            skLineSegment(sketch, "E463", {"start": v(544.88, 23.36) * mm, "end": v(544.88, 24.12) * mm});
            skLineSegment(sketch, "E464", {"start": v(544.88, 24.12) * mm, "end": v(559.86, 24.09) * mm});
            skLineSegment(sketch, "E465", {"start": v(559.86, 24.09) * mm, "end": v(559.86, 23.33) * mm});
            skLineSegment(sketch, "E466", {"start": v(563.03, 23.32) * mm, "end": v(563.03, 24.08) * mm});
            skLineSegment(sketch, "E467", {"start": v(563.03, 24.08) * mm, "end": v(577, 24.05) * mm});
            skLineSegment(sketch, "E468", {"start": v(577, 24.05) * mm, "end": v(577, 23.29) * mm});
            skLineSegment(sketch, "E469", {"start": v(580.17, 23.28) * mm, "end": v(580.17, 24.04) * mm});
            skLineSegment(sketch, "E470", {"start": v(580.17, 24.04) * mm, "end": v(593.17, 24) * mm});
            skLineSegment(sketch, "E471", {"start": v(593.17, 24) * mm, "end": v(593.17, 23.25) * mm});
            skLineSegment(sketch, "E472", {"start": v(596.34, 23.24) * mm, "end": v(596.35, 24) * mm});
            skLineSegment(sketch, "E473", {"start": v(596.35, 24) * mm, "end": v(608.44, 23.97) * mm});
            skLineSegment(sketch, "E474", {"start": v(608.44, 23.97) * mm, "end": v(608.44, 23.2) * mm});
            skLineSegment(sketch, "E475", {"start": v(611.61, 23.2) * mm, "end": v(611.61, 23.96) * mm});
            skLineSegment(sketch, "E476", {"start": v(611.61, 23.96) * mm, "end": v(622.85, 23.94) * mm});
            skLineSegment(sketch, "E477", {"start": v(622.85, 23.94) * mm, "end": v(622.85, 23.17) * mm});
            skLineSegment(sketch, "E478.MirrorCS", {"start": v(182.91, 24.23) * mm, "end": v(182.91, 23.47) * mm});
            skLineSegment(sketch, "E479.MirrorCS", {"start": v(608.43, 22.45) * mm, "end": v(608.44, 23.2) * mm});
            skLineSegment(sketch, "E480.MirrorCS", {"start": v(221.4, 24.14) * mm, "end": v(221.4, 23.38) * mm});
            skLineSegment(sketch, "E481.MirrorCS", {"start": v(559.86, 22.56) * mm, "end": v(559.86, 23.33) * mm});
            skLineSegment(sketch, "E482.MirrorCS", {"start": v(218.22, 23.38) * mm, "end": v(218.22, 24.15) * mm});
            skLineSegment(sketch, "E483.MirrorCS", {"start": v(291.98, 23.97) * mm, "end": v(291.98, 23.2) * mm});
            skLineSegment(sketch, "E484.MirrorCS", {"start": v(95.8, 23.68) * mm, "end": v(95.8, 24.44) * mm});
            skLineSegment(sketch, "E485.MirrorCS", {"start": v(50.06, 23.79) * mm, "end": v(50.06, 24.55) * mm});
            skLineSegment(sketch, "E486.MirrorCS", {"start": v(611.61, 23.2) * mm, "end": v(611.6, 22.44) * mm});
            skLineSegment(sketch, "E487.MirrorCS", {"start": v(596.34, 23.24) * mm, "end": v(596.34, 22.48) * mm});
            skLineSegment(sketch, "E488.MirrorCS", {"start": v(324.33, 23.9) * mm, "end": v(324.33, 23.13) * mm});
            skLineSegment(sketch, "E489.MirrorCS", {"start": v(580.17, 23.28) * mm, "end": v(580.17, 22.52) * mm});
            skLineSegment(sketch, "E490.MirrorCS", {"start": v(480.5, 22.75) * mm, "end": v(480.5, 23.52) * mm});
            skLineSegment(sketch, "E491.MirrorCS", {"start": v(407.7, 22.93) * mm, "end": v(407.7, 23.7) * mm});
            skLineSegment(sketch, "E492.MirrorCS", {"start": v(593.17, 22.48) * mm, "end": v(593.17, 23.25) * mm});
            skLineSegment(sketch, "E493.MirrorCS", {"start": v(483.67, 23.5) * mm, "end": v(483.67, 22.75) * mm});
            skLineSegment(sketch, "E494.MirrorCS", {"start": v(580.17, 22.52) * mm, "end": v(593.17, 22.48) * mm});
            skLineSegment(sketch, "E495.MirrorCS", {"start": v(522.46, 22.65) * mm, "end": v(522.47, 23.42) * mm});
            skLineSegment(sketch, "E496.MirrorCS", {"start": v(321.15, 23.14) * mm, "end": v(321.15, 23.9) * mm});
            skLineSegment(sketch, "E497.MirrorCS", {"start": v(457.62, 22.8) * mm, "end": v(457.62, 23.57) * mm});
            skLineSegment(sketch, "E498.MirrorCS", {"start": v(563.03, 23.32) * mm, "end": v(563.03, 22.56) * mm});
            skLineSegment(sketch, "E499.MirrorCS", {"start": v(383.68, 23.75) * mm, "end": v(383.68, 22.99) * mm});
            skLineSegment(sketch, "E500.MirrorCS", {"start": v(380.5, 23) * mm, "end": v(380.5, 23.76) * mm});
            skLineSegment(sketch, "E501.MirrorCS", {"start": v(505.26, 23.46) * mm, "end": v(505.26, 22.7) * mm});
            skLineSegment(sketch, "E502.MirrorCS", {"start": v(596.34, 22.48) * mm, "end": v(608.43, 22.45) * mm});
            skLineSegment(sketch, "E503.MirrorCS", {"start": v(544.87, 22.6) * mm, "end": v(559.86, 22.56) * mm});
            skLineSegment(sketch, "E504.MirrorCS", {"start": v(142.16, 24.33) * mm, "end": v(142.16, 23.57) * mm});
            skLineSegment(sketch, "E505.MirrorCS", {"start": v(138.99, 23.57) * mm, "end": v(138.99, 24.34) * mm});
            skLineSegment(sketch, "E506.MirrorCS", {"start": v(98.98, 24.43) * mm, "end": v(98.98, 23.67) * mm});
            skLineSegment(sketch, "E507.MirrorCS", {"start": v(53.23, 24.54) * mm, "end": v(53.23, 23.78) * mm});
            skLineSegment(sketch, "E508.MirrorCS", {"start": v(4.76, 24.66) * mm, "end": v(4.76, 23.9) * mm});
            skLineSegment(sketch, "E509.MirrorCS", {"start": v(179.74, 23.48) * mm, "end": v(179.74, 24.24) * mm});
            skLineSegment(sketch, "E510.MirrorCS", {"start": v(433.38, 22.87) * mm, "end": v(433.39, 23.63) * mm});
            skLineSegment(sketch, "E511.MirrorCS", {"start": v(544.88, 23.36) * mm, "end": v(544.87, 22.6) * mm});
            skLineSegment(sketch, "E512.MirrorCS", {"start": v(502.09, 22.7) * mm, "end": v(502.09, 23.46) * mm});
            skLineSegment(sketch, "E513.MirrorCS", {"start": v(288.8, 23.21) * mm, "end": v(288.8, 23.98) * mm});
            skLineSegment(sketch, "E514.MirrorCS", {"start": v(563.03, 22.56) * mm, "end": v(577, 22.52) * mm});
            skLineSegment(sketch, "E515.MirrorCS", {"start": v(254.53, 23.3) * mm, "end": v(254.53, 24.06) * mm});
            skLineSegment(sketch, "E516.MirrorCS", {"start": v(611.6, 22.44) * mm, "end": v(622.84, 22.41) * mm});
            skLineSegment(sketch, "E517.MirrorCS", {"start": v(525.64, 23.4) * mm, "end": v(525.64, 22.65) * mm});
            skLineSegment(sketch, "E518.MirrorCS", {"start": v(351.68, 23.06) * mm, "end": v(351.69, 23.83) * mm});
            skLineSegment(sketch, "E519.MirrorCS", {"start": v(410.88, 23.68) * mm, "end": v(410.88, 22.92) * mm});
            skLineSegment(sketch, "E520.MirrorCS", {"start": v(577, 22.52) * mm, "end": v(577, 23.29) * mm});
            skLineSegment(sketch, "E521.MirrorCS", {"start": v(257.7, 24.05) * mm, "end": v(257.7, 23.29) * mm});
            skLineSegment(sketch, "E522.MirrorCS", {"start": v(622.84, 22.41) * mm, "end": v(622.85, 23.17) * mm});
            skLineSegment(sketch, "E523.MirrorCS", {"start": v(354.86, 23.82) * mm, "end": v(354.86, 23.06) * mm});
            skLineSegment(sketch, "E524.MirrorCS", {"start": v(505.26, 22.7) * mm, "end": v(522.46, 22.65) * mm});
            skLineSegment(sketch, "E525.MirrorCS", {"start": v(436.56, 23.62) * mm, "end": v(436.56, 22.86) * mm});
            skLineSegment(sketch, "E526.MirrorCS", {"start": v(182.91, 23.47) * mm, "end": v(218.22, 23.38) * mm, "construction": true});
            skLineSegment(sketch, "E527.MirrorCS", {"start": v(460.8, 23.56) * mm, "end": v(460.8, 22.8) * mm});
            skLineSegment(sketch, "E528.MirrorCS", {"start": v(541.7, 22.6) * mm, "end": v(541.7, 23.37) * mm});
            skLineSegment(sketch, "E529.MirrorCS", {"start": v(525.64, 22.65) * mm, "end": v(541.7, 22.6) * mm});
            skLineSegment(sketch, "E530.MirrorCS", {"start": v(221.4, 23.38) * mm, "end": v(254.53, 23.3) * mm});
            skLineSegment(sketch, "E531.MirrorCS", {"start": v(383.68, 22.99) * mm, "end": v(407.7, 22.93) * mm});
            skLineSegment(sketch, "E532.MirrorCS", {"start": v(291.98, 23.2) * mm, "end": v(321.15, 23.14) * mm});
            skLineSegment(sketch, "E533.MirrorCS", {"start": v(436.56, 22.86) * mm, "end": v(457.62, 22.8) * mm});
            skLineSegment(sketch, "E534.MirrorCS", {"start": v(142.16, 23.57) * mm, "end": v(179.74, 23.48) * mm});
            skLineSegment(sketch, "E535.MirrorCS", {"start": v(53.23, 23.78) * mm, "end": v(95.8, 23.68) * mm});
            skLineSegment(sketch, "E536.MirrorCS", {"start": v(4.76, 23.9) * mm, "end": v(50.06, 23.79) * mm});
            skLineSegment(sketch, "E537.MirrorCS", {"start": v(354.86, 23.06) * mm, "end": v(380.5, 23) * mm});
            skLineSegment(sketch, "E538.MirrorCS", {"start": v(257.7, 23.29) * mm, "end": v(288.8, 23.21) * mm});
            skLineSegment(sketch, "E539.MirrorCS", {"start": v(483.67, 22.75) * mm, "end": v(502.09, 22.7) * mm});
            skLineSegment(sketch, "E540.MirrorCS", {"start": v(410.88, 22.92) * mm, "end": v(433.38, 22.87) * mm});
            skLineSegment(sketch, "E541.MirrorCS", {"start": v(182.91, 23.47) * mm, "end": v(218.22, 23.38) * mm});
            skLineSegment(sketch, "E542.MirrorCS", {"start": v(460.8, 22.8) * mm, "end": v(480.5, 22.75) * mm});
            skLineSegment(sketch, "E543.MirrorCS", {"start": v(324.33, 23.13) * mm, "end": v(351.68, 23.06) * mm});
            skLineSegment(sketch, "E544.MirrorCS", {"start": v(98.98, 23.67) * mm, "end": v(138.99, 23.57) * mm});
            skLineSegment(sketch, "E545", {"start": v(0, 28.2) * mm, "end": v(665.02, 28.2) * mm, "construction": true});
            skLineSegment(sketch, "E546.MirrorCS", {"start": v(218.2, 41.1) * mm, "end": v(218.21, 40.34) * mm});
            skLineSegment(sketch, "E547.MirrorCS", {"start": v(218.22, 39.58) * mm, "end": v(218.21, 40.34) * mm});
            skLineSegment(sketch, "E548.MirrorCS", {"start": v(182.91, 40.08) * mm, "end": v(182.92, 39.32) * mm});
            skLineSegment(sketch, "E549.MirrorCS", {"start": v(95.78, 55.24) * mm, "end": v(95.8, 54.47) * mm});
            skLineSegment(sketch, "E550.MirrorCS", {"start": v(50.04, 54.47) * mm, "end": v(50.05, 53.7) * mm});
            skLineSegment(sketch, "E551.MirrorCS", {"start": v(182.91, 40.08) * mm, "end": v(182.9, 40.85) * mm});
            skLineSegment(sketch, "E552.MirrorCS", {"start": v(218.21, 47.67) * mm, "end": v(218.2, 48.43) * mm});
            skLineSegment(sketch, "E553.MirrorCS", {"start": v(351.67, 49.27) * mm, "end": v(351.66, 50.04) * mm});
            skLineSegment(sketch, "E554.MirrorCS", {"start": v(354.84, 50.07) * mm, "end": v(354.85, 49.31) * mm});
            skLineSegment(sketch, "E555.MirrorCS", {"start": v(4.76, 38.8) * mm, "end": v(4.77, 38.04) * mm});
            skLineSegment(sketch, "E556.MirrorCS", {"start": v(324.3, 49.7) * mm, "end": v(324.31, 48.95) * mm});
            skLineSegment(sketch, "E557.MirrorCS", {"start": v(218.2, 49.2) * mm, "end": v(218.2, 48.43) * mm});
            skLineSegment(sketch, "E558.MirrorCS", {"start": v(53.23, 53.76) * mm, "end": v(53.21, 54.52) * mm});
            skLineSegment(sketch, "E559.MirrorCS", {"start": v(98.97, 54.53) * mm, "end": v(98.96, 55.29) * mm});
            skLineSegment(sketch, "E560.MirrorCS", {"start": v(324.32, 41.1) * mm, "end": v(324.31, 41.86) * mm});
            skLineSegment(sketch, "E561.MirrorCS", {"start": v(321.12, 50.43) * mm, "end": v(321.13, 49.67) * mm});
            skLineSegment(sketch, "E562.MirrorCS", {"start": v(541.65, 53.08) * mm, "end": v(541.66, 52.32) * mm});
            skLineSegment(sketch, "E563.MirrorCS", {"start": v(291.96, 49.32) * mm, "end": v(291.97, 48.56) * mm});
            skLineSegment(sketch, "E564.MirrorCS", {"start": v(95.8, 46.2) * mm, "end": v(95.8, 46.96) * mm});
            skLineSegment(sketch, "E565.MirrorCS", {"start": v(410.88, 41.73) * mm, "end": v(410.87, 42.49) * mm});
            skLineSegment(sketch, "E566.MirrorCS", {"start": v(522.42, 52.85) * mm, "end": v(522.43, 52.08) * mm});
            skLineSegment(sketch, "E567.MirrorCS", {"start": v(288.8, 48.52) * mm, "end": v(288.78, 49.28) * mm});
            skLineSegment(sketch, "E568.MirrorCS", {"start": v(544.84, 52.35) * mm, "end": v(544.85, 51.6) * mm});
            skLineSegment(sketch, "E569.MirrorCS", {"start": v(608.38, 53.88) * mm, "end": v(608.4, 53.12) * mm});
            skLineSegment(sketch, "E570.MirrorCS", {"start": v(611.6, 43.17) * mm, "end": v(611.6, 43.93) * mm});
            skLineSegment(sketch, "E571.MirrorCS", {"start": v(541.67, 51.55) * mm, "end": v(541.66, 52.32) * mm});
            skLineSegment(sketch, "E572.MirrorCS", {"start": v(182.9, 48.01) * mm, "end": v(182.9, 48.77) * mm});
            skLineSegment(sketch, "E573.MirrorCS", {"start": v(53.23, 46.45) * mm, "end": v(53.24, 45.7) * mm});
            skLineSegment(sketch, "E574.MirrorCS", {"start": v(182.91, 32.16) * mm, "end": v(182.91, 32.92) * mm});
            skLineSegment(sketch, "E575.MirrorCS", {"start": v(480.5, 41.46) * mm, "end": v(480.49, 42.23) * mm});
            skLineSegment(sketch, "E576.MirrorCS", {"start": v(179.72, 48.73) * mm, "end": v(179.73, 47.97) * mm});
            skLineSegment(sketch, "E577.MirrorCS", {"start": v(257.69, 48.9) * mm, "end": v(257.7, 48.15) * mm});
            skLineSegment(sketch, "E578.MirrorCS", {"start": v(50.06, 45.65) * mm, "end": v(50.05, 46.42) * mm});
            skLineSegment(sketch, "E579.MirrorCS", {"start": v(179.74, 32.91) * mm, "end": v(179.74, 32.15) * mm});
            skLineSegment(sketch, "E580.MirrorCS", {"start": v(50.05, 39.89) * mm, "end": v(50.06, 39.13) * mm});
            skLineSegment(sketch, "E581.MirrorCS", {"start": v(480.45, 52.34) * mm, "end": v(480.46, 51.58) * mm});
            skLineSegment(sketch, "E582.MirrorCS", {"start": v(608.4, 52.35) * mm, "end": v(608.4, 53.12) * mm});
            skLineSegment(sketch, "E583.MirrorCS", {"start": v(522.44, 51.32) * mm, "end": v(522.43, 52.08) * mm});
            skLineSegment(sketch, "E584.MirrorCS", {"start": v(4.76, 45.87) * mm, "end": v(4.77, 45.11) * mm});
            skLineSegment(sketch, "E585.MirrorCS", {"start": v(354.84, 50.07) * mm, "end": v(354.83, 50.84) * mm});
            skLineSegment(sketch, "E586.MirrorCS", {"start": v(53.23, 46.45) * mm, "end": v(53.22, 47.22) * mm});
            skLineSegment(sketch, "E587.MirrorCS", {"start": v(324.32, 41.1) * mm, "end": v(324.33, 40.34) * mm});
            skLineSegment(sketch, "E588.MirrorCS", {"start": v(139, 39) * mm, "end": v(138.99, 39.77) * mm});
            skLineSegment(sketch, "E589.MirrorCS", {"start": v(291.97, 40.87) * mm, "end": v(291.97, 41.63) * mm});
            skLineSegment(sketch, "E590.MirrorCS", {"start": v(4.76, 45.87) * mm, "end": v(4.75, 46.63) * mm});
            skLineSegment(sketch, "E591.MirrorCS", {"start": v(4.76, 52.94) * mm, "end": v(4.77, 52.18) * mm});
            skLineSegment(sketch, "E592.MirrorCS", {"start": v(50.06, 52.94) * mm, "end": v(50.05, 53.7) * mm});
            skLineSegment(sketch, "E593.MirrorCS", {"start": v(53.23, 53.76) * mm, "end": v(53.24, 53) * mm});
            skLineSegment(sketch, "E594.MirrorCS", {"start": v(95.8, 53.71) * mm, "end": v(95.8, 54.47) * mm});
            skLineSegment(sketch, "E595.MirrorCS", {"start": v(98.97, 54.53) * mm, "end": v(98.98, 53.76) * mm});
            skLineSegment(sketch, "E596.MirrorCS", {"start": v(351.65, 50.8) * mm, "end": v(351.66, 50.04) * mm});
            skLineSegment(sketch, "E597.MirrorCS", {"start": v(98.98, 39.48) * mm, "end": v(98.99, 38.72) * mm});
            skLineSegment(sketch, "E598.MirrorCS", {"start": v(179.74, 31.39) * mm, "end": v(179.74, 32.15) * mm});
            skLineSegment(sketch, "E599.MirrorCS", {"start": v(257.69, 48.9) * mm, "end": v(257.68, 49.67) * mm});
            skLineSegment(sketch, "E600.MirrorCS", {"start": v(380.5, 49.62) * mm, "end": v(380.48, 50.38) * mm});
            skLineSegment(sketch, "E601.MirrorCS", {"start": v(257.7, 40.62) * mm, "end": v(257.7, 39.86) * mm});
            skLineSegment(sketch, "E602.MirrorCS", {"start": v(410.88, 41.73) * mm, "end": v(410.88, 40.96) * mm});
            skLineSegment(sketch, "E603.MirrorCS", {"start": v(50.06, 38.37) * mm, "end": v(50.06, 39.13) * mm});
            skLineSegment(sketch, "E604.MirrorCS", {"start": v(480.47, 50.82) * mm, "end": v(480.46, 51.58) * mm});
            skLineSegment(sketch, "E605.MirrorCS", {"start": v(50.05, 47.18) * mm, "end": v(50.05, 46.42) * mm});
            skLineSegment(sketch, "E606.MirrorCS", {"start": v(221.39, 40.36) * mm, "end": v(221.38, 41.12) * mm});
            skLineSegment(sketch, "E607.MirrorCS", {"start": v(291.97, 40.87) * mm, "end": v(291.98, 40.1) * mm});
            skLineSegment(sketch, "E608.MirrorCS", {"start": v(324.3, 49.7) * mm, "end": v(324.3, 50.47) * mm});
            skLineSegment(sketch, "E609.MirrorCS", {"start": v(608.42, 43.9) * mm, "end": v(608.42, 43.15) * mm});
            skLineSegment(sketch, "E610.MirrorCS", {"start": v(182.9, 48.01) * mm, "end": v(182.91, 47.25) * mm});
            skLineSegment(sketch, "E611.MirrorCS", {"start": v(380.47, 51.14) * mm, "end": v(380.48, 50.38) * mm});
            skLineSegment(sketch, "E612.MirrorCS", {"start": v(95.8, 47.73) * mm, "end": v(95.8, 46.96) * mm});
            skLineSegment(sketch, "E613.MirrorCS", {"start": v(4.76, 38.8) * mm, "end": v(4.76, 39.56) * mm});
            skLineSegment(sketch, "E614.MirrorCS", {"start": v(4.76, 52.94) * mm, "end": v(4.75, 53.7) * mm});
            skLineSegment(sketch, "E615.MirrorCS", {"start": v(291.96, 49.32) * mm, "end": v(291.95, 50.08) * mm});
            skLineSegment(sketch, "E616.MirrorCS", {"start": v(53.23, 39.15) * mm, "end": v(53.23, 39.91) * mm});
            skLineSegment(sketch, "E617.MirrorCS", {"start": v(611.6, 43.17) * mm, "end": v(611.6, 42.4) * mm});
            skLineSegment(sketch, "E618.MirrorCS", {"start": v(288.77, 50.04) * mm, "end": v(288.78, 49.28) * mm});
            skLineSegment(sketch, "E619.MirrorCS", {"start": v(321.14, 48.9) * mm, "end": v(321.13, 49.67) * mm});
            skLineSegment(sketch, "E620.MirrorCS", {"start": v(480.48, 42.99) * mm, "end": v(480.49, 42.23) * mm});
            skLineSegment(sketch, "E621.MirrorCS", {"start": v(98.98, 39.48) * mm, "end": v(98.97, 40.24) * mm});
            skLineSegment(sketch, "E622.MirrorCS", {"start": v(221.39, 40.36) * mm, "end": v(221.4, 39.6) * mm});
            skLineSegment(sketch, "E623.MirrorCS", {"start": v(608.43, 42.39) * mm, "end": v(608.42, 43.15) * mm});
            skLineSegment(sketch, "E624.MirrorCS", {"start": v(257.7, 40.62) * mm, "end": v(257.7, 41.38) * mm});
            skLineSegment(sketch, "E625.MirrorCS", {"start": v(138.98, 40.53) * mm, "end": v(138.99, 39.77) * mm});
            skLineSegment(sketch, "E626.MirrorCS", {"start": v(580.09, 62.61) * mm, "end": v(580.08, 63.37) * mm});
            skLineSegment(sketch, "E627.MirrorCS", {"start": v(218.2, 55.77) * mm, "end": v(218.19, 56.53) * mm});
            skLineSegment(sketch, "E628.MirrorCS", {"start": v(95.8, 31.19) * mm, "end": v(95.8, 31.95) * mm});
            skLineSegment(sketch, "E629.MirrorCS", {"start": v(142.16, 39.8) * mm, "end": v(142.16, 40.55) * mm});
            skLineSegment(sketch, "E630.MirrorCS", {"start": v(576.98, 43.68) * mm, "end": v(576.98, 42.92) * mm});
            skLineSegment(sketch, "E631.MirrorCS", {"start": v(502.04, 52.6) * mm, "end": v(502.05, 51.84) * mm});
            skLineSegment(sketch, "E632.MirrorCS", {"start": v(436.53, 51.05) * mm, "end": v(436.54, 50.3) * mm});
            skLineSegment(sketch, "E633.MirrorCS", {"start": v(544.84, 52.35) * mm, "end": v(544.83, 53.12) * mm});
            skLineSegment(sketch, "E634.MirrorCS", {"start": v(460.76, 51.34) * mm, "end": v(460.76, 52.1) * mm});
            skLineSegment(sketch, "E635.MirrorCS", {"start": v(433.37, 50.25) * mm, "end": v(433.36, 51.02) * mm});
            skLineSegment(sketch, "E636.MirrorCS", {"start": v(576.9, 63.32) * mm, "end": v(576.91, 62.56) * mm});
            skLineSegment(sketch, "E637.MirrorCS", {"start": v(179.74, 39.3) * mm, "end": v(179.74, 40.06) * mm});
            skLineSegment(sketch, "E638.MirrorCS", {"start": v(433.35, 51.78) * mm, "end": v(433.36, 51.02) * mm});
            skLineSegment(sketch, "E639.MirrorCS", {"start": v(53.23, 31.85) * mm, "end": v(53.23, 31.08) * mm});
            skLineSegment(sketch, "E640.MirrorCS", {"start": v(483.64, 51.62) * mm, "end": v(483.63, 52.38) * mm});
            skLineSegment(sketch, "E641.MirrorCS", {"start": v(436.53, 51.05) * mm, "end": v(436.52, 51.82) * mm});
            skLineSegment(sketch, "E642.MirrorCS", {"start": v(410.86, 50.75) * mm, "end": v(410.87, 49.98) * mm});
            skLineSegment(sketch, "E643.MirrorCS", {"start": v(50.06, 31.08) * mm, "end": v(50.06, 31.84) * mm});
            skLineSegment(sketch, "E644.MirrorCS", {"start": v(457.6, 42.82) * mm, "end": v(457.61, 42.06) * mm});
            skLineSegment(sketch, "E645.MirrorCS", {"start": v(138.99, 32.81) * mm, "end": v(138.99, 32.05) * mm});
            skLineSegment(sketch, "E646.MirrorCS", {"start": v(383.63, 59.3) * mm, "end": v(383.62, 60.07) * mm});
            skLineSegment(sketch, "E647.MirrorCS", {"start": v(291.94, 57.77) * mm, "end": v(291.92, 58.53) * mm});
            skLineSegment(sketch, "E648.MirrorCS", {"start": v(383.66, 50.42) * mm, "end": v(383.66, 49.66) * mm});
            skLineSegment(sketch, "E649.MirrorCS", {"start": v(98.97, 47) * mm, "end": v(98.97, 47.76) * mm});
            skLineSegment(sketch, "E650.MirrorCS", {"start": v(457.62, 41.3) * mm, "end": v(457.61, 42.06) * mm});
            skLineSegment(sketch, "E651.MirrorCS", {"start": v(563.02, 42.82) * mm, "end": v(563.01, 43.58) * mm});
            skLineSegment(sketch, "E652.MirrorCS", {"start": v(98.98, 31.96) * mm, "end": v(98.98, 32.72) * mm});
            skLineSegment(sketch, "E653.MirrorCS", {"start": v(611.57, 53.15) * mm, "end": v(611.58, 52.4) * mm});
            skLineSegment(sketch, "E654.MirrorCS", {"start": v(254.52, 41.36) * mm, "end": v(254.52, 40.6) * mm});
            skLineSegment(sketch, "E655.MirrorCS", {"start": v(4.76, 31.73) * mm, "end": v(4.76, 30.97) * mm});
            skLineSegment(sketch, "E656.MirrorCS", {"start": v(53.23, 31.85) * mm, "end": v(53.23, 32.6) * mm});
            skLineSegment(sketch, "E657.MirrorCS", {"start": v(525.6, 52.12) * mm, "end": v(525.61, 51.36) * mm});
            skLineSegment(sketch, "E658.MirrorCS", {"start": v(142.16, 39.8) * mm, "end": v(142.17, 39.03) * mm});
            skLineSegment(sketch, "E659.MirrorCS", {"start": v(611.6, 43.93) * mm, "end": v(622.83, 44.01) * mm});
            skLineSegment(sketch, "E660.MirrorCS", {"start": v(95.8, 40.22) * mm, "end": v(95.8, 39.46) * mm});
            skLineSegment(sketch, "E661.MirrorCS", {"start": v(4.76, 31.73) * mm, "end": v(4.76, 32.5) * mm});
            skLineSegment(sketch, "E662.MirrorCS", {"start": v(182.89, 55.94) * mm, "end": v(182.9, 55.17) * mm});
            skLineSegment(sketch, "E663.MirrorCS", {"start": v(53.23, 39.15) * mm, "end": v(53.24, 38.39) * mm});
            skLineSegment(sketch, "E664.MirrorCS", {"start": v(483.64, 51.62) * mm, "end": v(483.65, 50.86) * mm});
            skLineSegment(sketch, "E665.MirrorCS", {"start": v(611.57, 53.15) * mm, "end": v(611.56, 53.92) * mm});
            skLineSegment(sketch, "E666.MirrorCS", {"start": v(179.74, 47.21) * mm, "end": v(179.73, 47.97) * mm});
            skLineSegment(sketch, "E667.MirrorCS", {"start": v(608.34, 63.85) * mm, "end": v(608.35, 63.09) * mm});
            skLineSegment(sketch, "E668.MirrorCS", {"start": v(522.38, 62.4) * mm, "end": v(522.4, 61.64) * mm});
            skLineSegment(sketch, "E669.MirrorCS", {"start": v(525.63, 42.55) * mm, "end": v(525.62, 43.31) * mm});
            skLineSegment(sketch, "E670.MirrorCS", {"start": v(182.89, 55.94) * mm, "end": v(182.88, 56.7) * mm});
            skLineSegment(sketch, "E671.MirrorCS", {"start": v(218.18, 57.3) * mm, "end": v(218.19, 56.53) * mm});
            skLineSegment(sketch, "E672.MirrorCS", {"start": v(179.73, 40.82) * mm, "end": v(179.74, 40.06) * mm});
            skLineSegment(sketch, "E673.MirrorCS", {"start": v(436.55, 41.9) * mm, "end": v(436.55, 42.67) * mm});
            skLineSegment(sketch, "E674.MirrorCS", {"start": v(562.95, 62.32) * mm, "end": v(562.97, 61.56) * mm});
            skLineSegment(sketch, "E675.MirrorCS", {"start": v(622.84, 42.49) * mm, "end": v(622.83, 43.25) * mm});
            skLineSegment(sketch, "E676.MirrorCS", {"start": v(525.6, 52.12) * mm, "end": v(525.6, 52.88) * mm});
            skLineSegment(sketch, "E677.MirrorCS", {"start": v(580.13, 52.78) * mm, "end": v(580.14, 52.02) * mm});
            skLineSegment(sketch, "E678.MirrorCS", {"start": v(142.16, 32.06) * mm, "end": v(142.16, 32.82) * mm});
            skLineSegment(sketch, "E679.MirrorCS", {"start": v(95.81, 38.7) * mm, "end": v(95.8, 39.46) * mm});
            skLineSegment(sketch, "E680.MirrorCS", {"start": v(142.15, 47.52) * mm, "end": v(142.15, 48.28) * mm});
            skLineSegment(sketch, "E681.MirrorCS", {"start": v(576.94, 53.5) * mm, "end": v(576.95, 52.74) * mm});
            skLineSegment(sketch, "E682.MirrorCS", {"start": v(502.06, 51.08) * mm, "end": v(502.05, 51.84) * mm});
            skLineSegment(sketch, "E683.MirrorCS", {"start": v(182.91, 32.16) * mm, "end": v(182.92, 31.4) * mm});
            skLineSegment(sketch, "E684.MirrorCS", {"start": v(522.45, 43.3) * mm, "end": v(522.45, 42.53) * mm});
            skLineSegment(sketch, "E685.MirrorCS", {"start": v(410.86, 50.75) * mm, "end": v(410.85, 51.5) * mm});
            skLineSegment(sketch, "E686.MirrorCS", {"start": v(291.94, 57.77) * mm, "end": v(291.95, 57) * mm});
            skLineSegment(sketch, "E687.MirrorCS", {"start": v(436.5, 60.2) * mm, "end": v(436.51, 59.44) * mm});
            skLineSegment(sketch, "E688.MirrorCS", {"start": v(254.53, 39.84) * mm, "end": v(254.52, 40.6) * mm});
            skLineSegment(sketch, "E689.MirrorCS", {"start": v(407.7, 40.94) * mm, "end": v(407.7, 41.7) * mm});
            skLineSegment(sketch, "E690.MirrorCS", {"start": v(525.63, 42.55) * mm, "end": v(525.63, 41.79) * mm});
            skLineSegment(sketch, "E691.MirrorCS", {"start": v(611.6, 42.4) * mm, "end": v(622.84, 42.49) * mm});
            skLineSegment(sketch, "E692.MirrorCS", {"start": v(576.96, 51.98) * mm, "end": v(576.95, 52.74) * mm});
            skLineSegment(sketch, "E693.MirrorCS", {"start": v(436.5, 60.2) * mm, "end": v(436.49, 60.96) * mm});
            skLineSegment(sketch, "E694.MirrorCS", {"start": v(179.7, 56.65) * mm, "end": v(179.72, 55.88) * mm});
            skLineSegment(sketch, "E695.MirrorCS", {"start": v(142.15, 47.52) * mm, "end": v(142.16, 46.76) * mm});
            skLineSegment(sketch, "E696.MirrorCS", {"start": v(95.8, 32.71) * mm, "end": v(95.8, 31.95) * mm});
            skLineSegment(sketch, "E697.MirrorCS", {"start": v(142.16, 32.06) * mm, "end": v(142.17, 31.3) * mm});
            skLineSegment(sketch, "E698.MirrorCS", {"start": v(383.66, 50.42) * mm, "end": v(383.65, 51.18) * mm});
            skLineSegment(sketch, "E699.MirrorCS", {"start": v(460.76, 51.34) * mm, "end": v(460.77, 50.58) * mm});
            skLineSegment(sketch, "E700.MirrorCS", {"start": v(593.07, 63.6) * mm, "end": v(593.09, 62.83) * mm});
            skLineSegment(sketch, "E701.MirrorCS", {"start": v(139, 31.29) * mm, "end": v(138.99, 32.05) * mm});
            skLineSegment(sketch, "E702.MirrorCS", {"start": v(407.7, 42.46) * mm, "end": v(407.7, 41.7) * mm});
            skLineSegment(sketch, "E703.MirrorCS", {"start": v(522.46, 41.77) * mm, "end": v(522.45, 42.53) * mm});
            skLineSegment(sketch, "E704.MirrorCS", {"start": v(563, 52.57) * mm, "end": v(563, 51.8) * mm});
            skLineSegment(sketch, "E705.MirrorCS", {"start": v(522.4, 60.88) * mm, "end": v(522.4, 61.64) * mm});
            skLineSegment(sketch, "E706.MirrorCS", {"start": v(622.83, 44.01) * mm, "end": v(622.83, 43.25) * mm});
            skLineSegment(sketch, "E707.MirrorCS", {"start": v(98.97, 47) * mm, "end": v(98.98, 46.24) * mm});
            skLineSegment(sketch, "E708.MirrorCS", {"start": v(383.63, 59.3) * mm, "end": v(383.64, 58.55) * mm});
            skLineSegment(sketch, "E709.MirrorCS", {"start": v(608.36, 62.32) * mm, "end": v(608.35, 63.09) * mm});
            skLineSegment(sketch, "E710.MirrorCS", {"start": v(98.98, 31.96) * mm, "end": v(98.98, 31.2) * mm});
            skLineSegment(sketch, "E711.MirrorCS", {"start": v(559.83, 51.77) * mm, "end": v(559.82, 52.53) * mm});
            skLineSegment(sketch, "E712.MirrorCS", {"start": v(559.8, 53.3) * mm, "end": v(559.82, 52.53) * mm});
            skLineSegment(sketch, "E713.MirrorCS", {"start": v(380.47, 58.5) * mm, "end": v(380.45, 59.26) * mm});
            skLineSegment(sketch, "E714.MirrorCS", {"start": v(505.2, 61.35) * mm, "end": v(505.2, 60.6) * mm});
            skLineSegment(sketch, "E715.MirrorCS", {"start": v(596.27, 62.12) * mm, "end": v(608.36, 62.32) * mm});
            skLineSegment(sketch, "E716.MirrorCS", {"start": v(291.98, 32.42) * mm, "end": v(291.98, 31.66) * mm});
            skLineSegment(sketch, "E717.MirrorCS", {"start": v(502.08, 41.62) * mm, "end": v(502.08, 42.38) * mm});
            skLineSegment(sketch, "E718.MirrorCS", {"start": v(596.33, 43.06) * mm, "end": v(596.34, 42.3) * mm});
            skLineSegment(sketch, "E719.MirrorCS", {"start": v(221.38, 48.47) * mm, "end": v(221.37, 49.23) * mm});
            skLineSegment(sketch, "E720.MirrorCS", {"start": v(257.67, 57.2) * mm, "end": v(257.66, 57.95) * mm});
            skLineSegment(sketch, "E721.MirrorCS", {"start": v(596.33, 43.06) * mm, "end": v(596.32, 43.82) * mm});
            skLineSegment(sketch, "E722.MirrorCS", {"start": v(354.85, 41.32) * mm, "end": v(354.86, 40.56) * mm});
            skLineSegment(sketch, "E723.MirrorCS", {"start": v(142.14, 55.25) * mm, "end": v(142.13, 56.01) * mm});
            skLineSegment(sketch, "E724.MirrorCS", {"start": v(502.03, 60.54) * mm, "end": v(502.02, 61.3) * mm});
            skLineSegment(sketch, "E725.MirrorCS", {"start": v(596.26, 62.88) * mm, "end": v(596.27, 62.12) * mm});
            skLineSegment(sketch, "E726.MirrorCS", {"start": v(324.28, 58.31) * mm, "end": v(324.27, 59.07) * mm});
            skLineSegment(sketch, "E727.MirrorCS", {"start": v(596.32, 43.82) * mm, "end": v(608.42, 43.9) * mm});
            skLineSegment(sketch, "E728.MirrorCS", {"start": v(351.67, 42.06) * mm, "end": v(351.68, 41.3) * mm});
            skLineSegment(sketch, "E729.MirrorCS", {"start": v(483.66, 42.25) * mm, "end": v(483.67, 41.49) * mm});
            skLineSegment(sketch, "E730.MirrorCS", {"start": v(580.12, 53.54) * mm, "end": v(593.12, 53.7) * mm});
            skLineSegment(sketch, "E731.MirrorCS", {"start": v(593.1, 62.07) * mm, "end": v(593.09, 62.83) * mm});
            skLineSegment(sketch, "E732.MirrorCS", {"start": v(596.26, 62.88) * mm, "end": v(596.25, 63.64) * mm});
            skLineSegment(sketch, "E733.MirrorCS", {"start": v(351.68, 40.54) * mm, "end": v(351.68, 41.3) * mm});
            skLineSegment(sketch, "E734.MirrorCS", {"start": v(580.16, 42.94) * mm, "end": v(580.16, 42.18) * mm});
            skLineSegment(sketch, "E735.MirrorCS", {"start": v(622.81, 52.53) * mm, "end": v(622.8, 53.29) * mm});
            skLineSegment(sketch, "E736.MirrorCS", {"start": v(596.25, 63.64) * mm, "end": v(608.34, 63.85) * mm});
            skLineSegment(sketch, "E737.MirrorCS", {"start": v(483.6, 60.99) * mm, "end": v(483.62, 60.23) * mm});
            skLineSegment(sketch, "E738.MirrorCS", {"start": v(580.1, 61.85) * mm, "end": v(593.1, 62.07) * mm});
            skLineSegment(sketch, "E739.MirrorCS", {"start": v(611.53, 63.14) * mm, "end": v(611.51, 63.9) * mm});
            skLineSegment(sketch, "E740.MirrorCS", {"start": v(505.25, 42.4) * mm, "end": v(505.25, 43.17) * mm});
            skLineSegment(sketch, "E741.MirrorCS", {"start": v(288.8, 41.6) * mm, "end": v(288.8, 40.85) * mm});
            skLineSegment(sketch, "E742.MirrorCS", {"start": v(559.84, 43.56) * mm, "end": v(559.84, 42.8) * mm});
            skLineSegment(sketch, "E743.MirrorCS", {"start": v(559.85, 42.04) * mm, "end": v(559.84, 42.8) * mm});
            skLineSegment(sketch, "E744.MirrorCS", {"start": v(218.22, 31.48) * mm, "end": v(218.22, 32.24) * mm});
            skLineSegment(sketch, "E745.MirrorCS", {"start": v(562.97, 61.56) * mm, "end": v(576.93, 61.8) * mm});
            skLineSegment(sketch, "E746.MirrorCS", {"start": v(324.28, 58.31) * mm, "end": v(324.3, 57.55) * mm});
            skLineSegment(sketch, "E747.MirrorCS", {"start": v(221.38, 48.47) * mm, "end": v(221.39, 47.7) * mm});
            skLineSegment(sketch, "E748.MirrorCS", {"start": v(622.8, 54.05) * mm, "end": v(622.8, 53.29) * mm});
            skLineSegment(sketch, "E749.MirrorCS", {"start": v(321.15, 40.32) * mm, "end": v(321.14, 41.08) * mm});
            skLineSegment(sketch, "E750.MirrorCS", {"start": v(563.01, 43.58) * mm, "end": v(576.98, 43.68) * mm});
            skLineSegment(sketch, "E751.MirrorCS", {"start": v(563.02, 42.82) * mm, "end": v(563.03, 42.06) * mm});
            skLineSegment(sketch, "E752.MirrorCS", {"start": v(576.93, 61.8) * mm, "end": v(576.91, 62.56) * mm});
            skLineSegment(sketch, "E753.MirrorCS", {"start": v(380.44, 60.02) * mm, "end": v(380.45, 59.26) * mm});
            skLineSegment(sketch, "E754.MirrorCS", {"start": v(407.67, 51.47) * mm, "end": v(407.68, 50.7) * mm});
            skLineSegment(sketch, "E755.MirrorCS", {"start": v(460.79, 42.08) * mm, "end": v(460.8, 41.32) * mm});
            skLineSegment(sketch, "E756.MirrorCS", {"start": v(383.67, 41.53) * mm, "end": v(383.67, 42.3) * mm});
            skLineSegment(sketch, "E757.MirrorCS", {"start": v(563.03, 42.06) * mm, "end": v(576.99, 42.16) * mm});
            skLineSegment(sketch, "E758.MirrorCS", {"start": v(580.09, 62.61) * mm, "end": v(580.1, 61.85) * mm});
            skLineSegment(sketch, "E759.MirrorCS", {"start": v(480.44, 60.17) * mm, "end": v(480.43, 60.94) * mm});
            skLineSegment(sketch, "E760.MirrorCS", {"start": v(525.57, 61.7) * mm, "end": v(525.56, 62.46) * mm});
            skLineSegment(sketch, "E761.MirrorCS", {"start": v(505.2, 61.35) * mm, "end": v(505.18, 62.11) * mm});
            skLineSegment(sketch, "E762.MirrorCS", {"start": v(407.7, 49.95) * mm, "end": v(407.68, 50.7) * mm});
            skLineSegment(sketch, "E763.MirrorCS", {"start": v(254.52, 48.1) * mm, "end": v(254.51, 48.87) * mm});
            skLineSegment(sketch, "E764.MirrorCS", {"start": v(593.12, 53.7) * mm, "end": v(593.13, 52.93) * mm});
            skLineSegment(sketch, "E765.MirrorCS", {"start": v(611.58, 52.4) * mm, "end": v(622.81, 52.53) * mm});
            skLineSegment(sketch, "E766.MirrorCS", {"start": v(380.5, 42.27) * mm, "end": v(380.5, 41.5) * mm});
            skLineSegment(sketch, "E767.MirrorCS", {"start": v(576.99, 42.16) * mm, "end": v(576.98, 42.92) * mm});
            skLineSegment(sketch, "E768.MirrorCS", {"start": v(179.73, 55.12) * mm, "end": v(179.72, 55.88) * mm});
            skLineSegment(sketch, "E769.MirrorCS", {"start": v(142.14, 55.25) * mm, "end": v(142.16, 54.5) * mm});
            skLineSegment(sketch, "E770.MirrorCS", {"start": v(433.37, 42.65) * mm, "end": v(433.38, 41.89) * mm});
            skLineSegment(sketch, "E771.MirrorCS", {"start": v(541.7, 41.9) * mm, "end": v(541.69, 42.67) * mm});
            skLineSegment(sketch, "E772.MirrorCS", {"start": v(596.3, 53.73) * mm, "end": v(608.38, 53.88) * mm});
            skLineSegment(sketch, "E773.MirrorCS", {"start": v(433.31, 60.9) * mm, "end": v(433.33, 60.14) * mm});
            skLineSegment(sketch, "E774.MirrorCS", {"start": v(580.14, 52.02) * mm, "end": v(593.14, 52.17) * mm});
            skLineSegment(sketch, "E775.MirrorCS", {"start": v(544.8, 62.02) * mm, "end": v(544.79, 62.78) * mm});
            skLineSegment(sketch, "E776.MirrorCS", {"start": v(544.8, 62.02) * mm, "end": v(544.81, 61.26) * mm});
            skLineSegment(sketch, "E777.MirrorCS", {"start": v(580.08, 63.37) * mm, "end": v(593.07, 63.6) * mm});
            skLineSegment(sketch, "E778.MirrorCS", {"start": v(596.31, 52.2) * mm, "end": v(608.4, 52.35) * mm});
            skLineSegment(sketch, "E779.MirrorCS", {"start": v(580.13, 52.78) * mm, "end": v(580.12, 53.54) * mm});
            skLineSegment(sketch, "E780.MirrorCS", {"start": v(138.97, 48.25) * mm, "end": v(138.98, 47.48) * mm});
            skLineSegment(sketch, "E781.MirrorCS", {"start": v(505.23, 51.88) * mm, "end": v(505.24, 51.12) * mm});
            skLineSegment(sketch, "E782.MirrorCS", {"start": v(483.66, 42.25) * mm, "end": v(483.65, 43.01) * mm});
            skLineSegment(sketch, "E783.MirrorCS", {"start": v(562.95, 62.32) * mm, "end": v(562.94, 63.08) * mm});
            skLineSegment(sketch, "E784.MirrorCS", {"start": v(562.94, 63.08) * mm, "end": v(576.9, 63.32) * mm});
            skLineSegment(sketch, "E785.MirrorCS", {"start": v(321.12, 57.5) * mm, "end": v(321.1, 58.26) * mm});
            skLineSegment(sketch, "E786.MirrorCS", {"start": v(457.57, 59.79) * mm, "end": v(457.56, 60.55) * mm});
            skLineSegment(sketch, "E787.MirrorCS", {"start": v(505.23, 51.88) * mm, "end": v(505.22, 52.64) * mm});
            skLineSegment(sketch, "E788.MirrorCS", {"start": v(541.68, 43.43) * mm, "end": v(541.69, 42.67) * mm});
            skLineSegment(sketch, "E789.MirrorCS", {"start": v(321.14, 41.84) * mm, "end": v(321.14, 41.08) * mm});
            skLineSegment(sketch, "E790.MirrorCS", {"start": v(502.07, 43.14) * mm, "end": v(502.08, 42.38) * mm});
            skLineSegment(sketch, "E791.MirrorCS", {"start": v(436.55, 41.9) * mm, "end": v(436.56, 41.15) * mm});
            skLineSegment(sketch, "E792.MirrorCS", {"start": v(596.3, 52.97) * mm, "end": v(596.31, 52.2) * mm});
            skLineSegment(sketch, "E793.MirrorCS", {"start": v(559.77, 63.03) * mm, "end": v(559.78, 62.27) * mm});
            skLineSegment(sketch, "E794.MirrorCS", {"start": v(457.55, 61.31) * mm, "end": v(457.56, 60.55) * mm});
            skLineSegment(sketch, "E795.MirrorCS", {"start": v(559.8, 61.5) * mm, "end": v(559.78, 62.27) * mm});
            skLineSegment(sketch, "E796.MirrorCS", {"start": v(460.79, 42.08) * mm, "end": v(460.78, 42.85) * mm});
            skLineSegment(sketch, "E797.MirrorCS", {"start": v(544.86, 42.69) * mm, "end": v(544.87, 41.93) * mm});
            skLineSegment(sketch, "E798.MirrorCS", {"start": v(544.86, 42.69) * mm, "end": v(544.86, 43.45) * mm});
            skLineSegment(sketch, "E799.MirrorCS", {"start": v(288.8, 40.08) * mm, "end": v(288.8, 40.85) * mm});
            skLineSegment(sketch, "E800.MirrorCS", {"start": v(433.38, 41.13) * mm, "end": v(433.38, 41.89) * mm});
            skLineSegment(sketch, "E801.MirrorCS", {"start": v(593.14, 52.17) * mm, "end": v(593.13, 52.93) * mm});
            skLineSegment(sketch, "E802.MirrorCS", {"start": v(596.3, 52.97) * mm, "end": v(596.3, 53.73) * mm});
            skLineSegment(sketch, "E803.MirrorCS", {"start": v(321.1, 59.02) * mm, "end": v(321.1, 58.26) * mm});
            skLineSegment(sketch, "E804.MirrorCS", {"start": v(502, 62.06) * mm, "end": v(502.02, 61.3) * mm});
            skLineSegment(sketch, "E805.MirrorCS", {"start": v(505.25, 42.4) * mm, "end": v(505.26, 41.64) * mm});
            skLineSegment(sketch, "E806.MirrorCS", {"start": v(50.06, 32.6) * mm, "end": v(50.06, 31.84) * mm});
            skLineSegment(sketch, "E807.MirrorCS", {"start": v(596.34, 42.3) * mm, "end": v(608.43, 42.39) * mm});
            skLineSegment(sketch, "E808.MirrorCS", {"start": v(611.56, 53.92) * mm, "end": v(622.8, 54.05) * mm});
            skLineSegment(sketch, "E809.MirrorCS", {"start": v(457.58, 52.07) * mm, "end": v(457.59, 51.3) * mm});
            skLineSegment(sketch, "E810.MirrorCS", {"start": v(483.6, 60.99) * mm, "end": v(483.6, 61.75) * mm});
            skLineSegment(sketch, "E811.MirrorCS", {"start": v(257.67, 57.2) * mm, "end": v(257.68, 56.43) * mm});
            skLineSegment(sketch, "E812.MirrorCS", {"start": v(593.15, 43.8) * mm, "end": v(593.16, 43.04) * mm});
            skLineSegment(sketch, "E813.MirrorCS", {"start": v(254.5, 49.63) * mm, "end": v(254.51, 48.87) * mm});
            skLineSegment(sketch, "E814.MirrorCS", {"start": v(563, 51.8) * mm, "end": v(576.96, 51.98) * mm});
            skLineSegment(sketch, "E815.MirrorCS", {"start": v(138.99, 46.72) * mm, "end": v(138.98, 47.48) * mm});
            skLineSegment(sketch, "E816.MirrorCS", {"start": v(525.57, 61.7) * mm, "end": v(525.58, 60.93) * mm});
            skLineSegment(sketch, "E817.MirrorCS", {"start": v(291.98, 32.42) * mm, "end": v(291.98, 33.18) * mm});
            skLineSegment(sketch, "E818.MirrorCS", {"start": v(354.85, 41.32) * mm, "end": v(354.85, 42.08) * mm});
            skLineSegment(sketch, "E819.MirrorCS", {"start": v(457.6, 50.54) * mm, "end": v(457.59, 51.3) * mm});
            skLineSegment(sketch, "E820.MirrorCS", {"start": v(611.53, 63.14) * mm, "end": v(611.54, 62.38) * mm});
            skLineSegment(sketch, "E821.MirrorCS", {"start": v(218.22, 33) * mm, "end": v(218.22, 32.24) * mm});
            skLineSegment(sketch, "E822.MirrorCS", {"start": v(383.67, 41.53) * mm, "end": v(383.68, 40.77) * mm});
            skLineSegment(sketch, "E823.MirrorCS", {"start": v(562.98, 53.33) * mm, "end": v(576.94, 53.5) * mm});
            skLineSegment(sketch, "E824.MirrorCS", {"start": v(563, 52.57) * mm, "end": v(562.98, 53.33) * mm});
            skLineSegment(sketch, "E825.MirrorCS", {"start": v(480.42, 61.7) * mm, "end": v(480.43, 60.94) * mm});
            skLineSegment(sketch, "E826.MirrorCS", {"start": v(580.16, 42.94) * mm, "end": v(580.15, 43.7) * mm});
            skLineSegment(sketch, "E827.MirrorCS", {"start": v(380.5, 40.74) * mm, "end": v(380.5, 41.5) * mm});
            skLineSegment(sketch, "E828.MirrorCS", {"start": v(221.4, 32.25) * mm, "end": v(221.4, 33.01) * mm});
            skLineSegment(sketch, "E829.MirrorCS", {"start": v(138.96, 55.96) * mm, "end": v(138.97, 55.2) * mm});
            skLineSegment(sketch, "E830.MirrorCS", {"start": v(593.16, 42.28) * mm, "end": v(593.16, 43.04) * mm});
            skLineSegment(sketch, "E831.MirrorCS", {"start": v(288.8, 31.65) * mm, "end": v(288.8, 32.41) * mm});
            skLineSegment(sketch, "E832.MirrorCS", {"start": v(580.16, 42.18) * mm, "end": v(593.16, 42.28) * mm});
            skLineSegment(sketch, "E833.MirrorCS", {"start": v(410.83, 59.77) * mm, "end": v(410.82, 60.53) * mm});
            skLineSegment(sketch, "E834.MirrorCS", {"start": v(354.81, 58.83) * mm, "end": v(354.83, 58.06) * mm});
            skLineSegment(sketch, "E835.MirrorCS", {"start": v(351.63, 59.53) * mm, "end": v(351.64, 58.77) * mm});
            skLineSegment(sketch, "E836.MirrorCS", {"start": v(257.7, 32.34) * mm, "end": v(257.7, 31.57) * mm});
            skLineSegment(sketch, "E837.MirrorCS", {"start": v(257.7, 32.34) * mm, "end": v(257.7, 33.1) * mm});
            skLineSegment(sketch, "E838.MirrorCS", {"start": v(460.73, 60.6) * mm, "end": v(460.75, 59.84) * mm});
            skLineSegment(sketch, "E839.MirrorCS", {"start": v(254.48, 57.9) * mm, "end": v(254.5, 57.14) * mm});
            skLineSegment(sketch, "E840.MirrorCS", {"start": v(221.4, 32.25) * mm, "end": v(221.4, 31.49) * mm});
            skLineSegment(sketch, "E841.MirrorCS", {"start": v(611.51, 63.9) * mm, "end": v(622.75, 64.09) * mm});
            skLineSegment(sketch, "E842.MirrorCS", {"start": v(351.65, 58.01) * mm, "end": v(351.64, 58.77) * mm});
            skLineSegment(sketch, "E843.MirrorCS", {"start": v(254.53, 31.57) * mm, "end": v(254.53, 32.33) * mm});
            skLineSegment(sketch, "E844.MirrorCS", {"start": v(138.98, 54.44) * mm, "end": v(138.97, 55.2) * mm});
            skLineSegment(sketch, "E845.MirrorCS", {"start": v(580.15, 43.7) * mm, "end": v(593.15, 43.8) * mm});
            skLineSegment(sketch, "E846.MirrorCS", {"start": v(460.73, 60.6) * mm, "end": v(460.72, 61.37) * mm});
            skLineSegment(sketch, "E847.MirrorCS", {"start": v(433.34, 59.38) * mm, "end": v(433.33, 60.14) * mm});
            skLineSegment(sketch, "E848.MirrorCS", {"start": v(288.78, 56.95) * mm, "end": v(288.76, 57.72) * mm});
            skLineSegment(sketch, "E849.MirrorCS", {"start": v(541.64, 61.2) * mm, "end": v(541.63, 61.96) * mm});
            skLineSegment(sketch, "E850.MirrorCS", {"start": v(288.75, 58.48) * mm, "end": v(288.76, 57.72) * mm});
            skLineSegment(sketch, "E851.MirrorCS", {"start": v(221.36, 56.58) * mm, "end": v(221.35, 57.34) * mm});
            skLineSegment(sketch, "E852.MirrorCS", {"start": v(541.61, 62.73) * mm, "end": v(541.63, 61.96) * mm});
            skLineSegment(sketch, "E853.MirrorCS", {"start": v(410.83, 59.77) * mm, "end": v(410.84, 59) * mm});
            skLineSegment(sketch, "E854.MirrorCS", {"start": v(622.77, 62.57) * mm, "end": v(622.76, 63.33) * mm});
            skLineSegment(sketch, "E855.MirrorCS", {"start": v(407.67, 58.95) * mm, "end": v(407.65, 59.71) * mm});
            skLineSegment(sketch, "E856.MirrorCS", {"start": v(611.54, 62.38) * mm, "end": v(622.77, 62.57) * mm});
            skLineSegment(sketch, "E857.MirrorCS", {"start": v(254.5, 56.38) * mm, "end": v(254.5, 57.14) * mm});
            skLineSegment(sketch, "E858.MirrorCS", {"start": v(254.53, 33.1) * mm, "end": v(254.53, 32.33) * mm});
            skLineSegment(sketch, "E859.MirrorCS", {"start": v(354.81, 58.83) * mm, "end": v(354.8, 59.59) * mm});
            skLineSegment(sketch, "E860.MirrorCS", {"start": v(407.64, 60.47) * mm, "end": v(407.65, 59.71) * mm});
            skLineSegment(sketch, "E861.MirrorCS", {"start": v(622.75, 64.09) * mm, "end": v(622.76, 63.33) * mm});
            skLineSegment(sketch, "E862.MirrorCS", {"start": v(221.36, 56.58) * mm, "end": v(221.38, 55.82) * mm});
            skLineSegment(sketch, "E863.MirrorCS", {"start": v(288.8, 33.17) * mm, "end": v(288.8, 32.41) * mm});
            skLineSegment(sketch, "E864.MirrorCS", {"start": v(407.7, 33.46) * mm, "end": v(407.7, 32.7) * mm});
            skLineSegment(sketch, "E865.MirrorCS", {"start": v(324.33, 32.5) * mm, "end": v(324.33, 33.26) * mm});
            skLineSegment(sketch, "E866.MirrorCS", {"start": v(182.91, 47.25) * mm, "end": v(218.21, 47.67) * mm, "construction": true});
            skLineSegment(sketch, "E867.MirrorCS", {"start": v(354.86, 32.57) * mm, "end": v(354.86, 31.8) * mm});
            skLineSegment(sketch, "E868.MirrorCS", {"start": v(351.69, 31.8) * mm, "end": v(351.69, 32.56) * mm});
            skLineSegment(sketch, "E869.MirrorCS", {"start": v(383.68, 32.64) * mm, "end": v(383.68, 33.4) * mm});
            skLineSegment(sketch, "E870.MirrorCS", {"start": v(324.33, 32.5) * mm, "end": v(324.33, 31.73) * mm});
            skLineSegment(sketch, "E871.MirrorCS", {"start": v(291.97, 48.56) * mm, "end": v(321.14, 48.9) * mm});
            skLineSegment(sketch, "E872.MirrorCS", {"start": v(321.15, 33.25) * mm, "end": v(321.15, 32.49) * mm});
            skLineSegment(sketch, "E873.MirrorCS", {"start": v(182.92, 39.32) * mm, "end": v(218.22, 39.58) * mm, "construction": true});
            skLineSegment(sketch, "E874.MirrorCS", {"start": v(324.3, 50.47) * mm, "end": v(351.65, 50.8) * mm});
            skLineSegment(sketch, "E875.MirrorCS", {"start": v(4.75, 53.7) * mm, "end": v(50.04, 54.47) * mm});
            skLineSegment(sketch, "E876.MirrorCS", {"start": v(182.9, 48.77) * mm, "end": v(218.2, 49.2) * mm, "construction": true});
            skLineSegment(sketch, "E877.MirrorCS", {"start": v(257.7, 48.15) * mm, "end": v(288.8, 48.52) * mm});
            skLineSegment(sketch, "E878.MirrorCS", {"start": v(53.21, 54.52) * mm, "end": v(95.78, 55.24) * mm});
            skLineSegment(sketch, "E879.MirrorCS", {"start": v(182.91, 32.92) * mm, "end": v(218.22, 33) * mm, "construction": true});
            skLineSegment(sketch, "E880.MirrorCS", {"start": v(354.86, 32.57) * mm, "end": v(354.86, 33.33) * mm});
            skLineSegment(sketch, "E881.MirrorCS", {"start": v(182.9, 55.17) * mm, "end": v(218.2, 55.77) * mm, "construction": true});
            skLineSegment(sketch, "E882.MirrorCS", {"start": v(182.9, 40.85) * mm, "end": v(218.2, 41.1) * mm, "construction": true});
            skLineSegment(sketch, "E883.MirrorCS", {"start": v(351.68, 33.32) * mm, "end": v(351.69, 32.56) * mm});
            skLineSegment(sketch, "E884.MirrorCS", {"start": v(182.92, 31.4) * mm, "end": v(218.22, 31.48) * mm, "construction": true});
            skLineSegment(sketch, "E885.MirrorCS", {"start": v(354.85, 49.31) * mm, "end": v(380.5, 49.62) * mm});
            skLineSegment(sketch, "E886.MirrorCS", {"start": v(410.88, 32.7) * mm, "end": v(410.88, 33.47) * mm});
            skLineSegment(sketch, "E887.MirrorCS", {"start": v(380.5, 33.4) * mm, "end": v(380.5, 32.63) * mm});
            skLineSegment(sketch, "E888.MirrorCS", {"start": v(321.15, 31.73) * mm, "end": v(321.15, 32.49) * mm});
            skLineSegment(sketch, "E889.MirrorCS", {"start": v(291.98, 31.66) * mm, "end": v(321.15, 31.73) * mm});
            skLineSegment(sketch, "E890.MirrorCS", {"start": v(436.54, 50.3) * mm, "end": v(457.6, 50.54) * mm});
            skLineSegment(sketch, "E891.MirrorCS", {"start": v(4.76, 39.56) * mm, "end": v(50.05, 39.89) * mm});
            skLineSegment(sketch, "E892.MirrorCS", {"start": v(354.86, 40.56) * mm, "end": v(380.5, 40.74) * mm});
            skLineSegment(sketch, "E893.MirrorCS", {"start": v(544.85, 51.6) * mm, "end": v(559.83, 51.77) * mm});
            skLineSegment(sketch, "E894.MirrorCS", {"start": v(544.86, 43.45) * mm, "end": v(559.84, 43.56) * mm});
            skLineSegment(sketch, "E895.MirrorCS", {"start": v(53.23, 39.91) * mm, "end": v(95.8, 40.22) * mm});
            skLineSegment(sketch, "E896.MirrorCS", {"start": v(483.67, 41.49) * mm, "end": v(502.08, 41.62) * mm});
            skLineSegment(sketch, "E897.MirrorCS", {"start": v(53.24, 45.7) * mm, "end": v(95.8, 46.2) * mm});
            skLineSegment(sketch, "E898.MirrorCS", {"start": v(354.83, 58.06) * mm, "end": v(380.47, 58.5) * mm});
            skLineSegment(sketch, "E899.MirrorCS", {"start": v(324.33, 33.26) * mm, "end": v(351.68, 33.32) * mm});
            skLineSegment(sketch, "E900.MirrorCS", {"start": v(142.16, 40.55) * mm, "end": v(179.73, 40.82) * mm});
            skLineSegment(sketch, "E901.MirrorCS", {"start": v(182.92, 39.32) * mm, "end": v(218.22, 39.58) * mm});
            skLineSegment(sketch, "E902.MirrorCS", {"start": v(460.76, 52.1) * mm, "end": v(480.45, 52.34) * mm});
            skLineSegment(sketch, "E903.MirrorCS", {"start": v(410.87, 49.98) * mm, "end": v(433.37, 50.25) * mm});
            skLineSegment(sketch, "E904.MirrorCS", {"start": v(544.79, 62.78) * mm, "end": v(559.77, 63.03) * mm});
            skLineSegment(sketch, "E905.MirrorCS", {"start": v(483.62, 60.23) * mm, "end": v(502.03, 60.54) * mm});
            skLineSegment(sketch, "E906.MirrorCS", {"start": v(460.8, 33.59) * mm, "end": v(480.5, 33.63) * mm});
            skLineSegment(sketch, "E907.MirrorCS", {"start": v(257.7, 31.57) * mm, "end": v(288.8, 31.65) * mm});
            skLineSegment(sketch, "E908.MirrorCS", {"start": v(142.17, 39.03) * mm, "end": v(179.74, 39.3) * mm});
            skLineSegment(sketch, "E909.MirrorCS", {"start": v(182.9, 48.77) * mm, "end": v(218.2, 49.2) * mm});
            skLineSegment(sketch, "E910.MirrorCS", {"start": v(525.61, 51.36) * mm, "end": v(541.67, 51.55) * mm});
            skLineSegment(sketch, "E911.MirrorCS", {"start": v(182.9, 55.17) * mm, "end": v(218.2, 55.77) * mm});
            skLineSegment(sketch, "E912.MirrorCS", {"start": v(182.91, 32.92) * mm, "end": v(218.22, 33) * mm});
            skLineSegment(sketch, "E913.MirrorCS", {"start": v(525.62, 43.31) * mm, "end": v(541.68, 43.43) * mm});
            skLineSegment(sketch, "E914.MirrorCS", {"start": v(505.24, 51.12) * mm, "end": v(522.44, 51.32) * mm});
            skLineSegment(sketch, "E915.MirrorCS", {"start": v(257.68, 49.67) * mm, "end": v(288.77, 50.04) * mm});
            skLineSegment(sketch, "E916.MirrorCS", {"start": v(221.38, 41.12) * mm, "end": v(254.52, 41.36) * mm});
            skLineSegment(sketch, "E917.MirrorCS", {"start": v(324.3, 57.55) * mm, "end": v(351.65, 58.01) * mm});
            skLineSegment(sketch, "E918.MirrorCS", {"start": v(291.92, 58.53) * mm, "end": v(321.1, 59.02) * mm});
            skLineSegment(sketch, "E919.MirrorCS", {"start": v(383.66, 49.66) * mm, "end": v(407.7, 49.95) * mm});
            skLineSegment(sketch, "E920.MirrorCS", {"start": v(221.39, 47.7) * mm, "end": v(254.52, 48.1) * mm});
            skLineSegment(sketch, "E921.MirrorCS", {"start": v(483.63, 52.38) * mm, "end": v(502.04, 52.6) * mm});
            skLineSegment(sketch, "E922.MirrorCS", {"start": v(383.67, 42.3) * mm, "end": v(407.7, 42.46) * mm});
            skLineSegment(sketch, "E923.MirrorCS", {"start": v(4.77, 45.11) * mm, "end": v(50.06, 45.65) * mm});
            skLineSegment(sketch, "E924.MirrorCS", {"start": v(505.22, 52.64) * mm, "end": v(522.42, 52.85) * mm});
            skLineSegment(sketch, "E925.MirrorCS", {"start": v(460.8, 41.32) * mm, "end": v(480.5, 41.46) * mm});
            skLineSegment(sketch, "E926.MirrorCS", {"start": v(324.33, 40.34) * mm, "end": v(351.68, 40.54) * mm});
            skLineSegment(sketch, "E927.MirrorCS", {"start": v(410.85, 51.5) * mm, "end": v(433.35, 51.78) * mm});
            skLineSegment(sketch, "E928.MirrorCS", {"start": v(291.97, 41.63) * mm, "end": v(321.14, 41.84) * mm});
            skLineSegment(sketch, "E929.MirrorCS", {"start": v(505.26, 33.7) * mm, "end": v(522.46, 33.73) * mm});
            skLineSegment(sketch, "E930.MirrorCS", {"start": v(0, 52.86) * mm, "end": v(648.16, 63.75) * mm, "construction": true});
            skLineSegment(sketch, "E931.MirrorCS", {"start": v(4.77, 52.18) * mm, "end": v(50.06, 52.94) * mm});
            skLineSegment(sketch, "E932.MirrorCS", {"start": v(53.24, 53) * mm, "end": v(95.8, 53.71) * mm});
            skLineSegment(sketch, "E933.MirrorCS", {"start": v(142.16, 54.5) * mm, "end": v(179.73, 55.12) * mm});
            skLineSegment(sketch, "E934.MirrorCS", {"start": v(460.78, 42.85) * mm, "end": v(480.48, 42.99) * mm});
            skLineSegment(sketch, "E935.MirrorCS", {"start": v(257.7, 39.86) * mm, "end": v(288.8, 40.08) * mm});
            skLineSegment(sketch, "E936.MirrorCS", {"start": v(410.88, 40.96) * mm, "end": v(433.38, 41.13) * mm});
            skLineSegment(sketch, "E937.MirrorCS", {"start": v(142.15, 48.28) * mm, "end": v(179.72, 48.73) * mm});
            skLineSegment(sketch, "E938.MirrorCS", {"start": v(182.91, 47.25) * mm, "end": v(218.21, 47.67) * mm});
            skLineSegment(sketch, "E939.MirrorCS", {"start": v(324.27, 59.07) * mm, "end": v(351.63, 59.53) * mm});
            skLineSegment(sketch, "E940.MirrorCS", {"start": v(182.88, 56.7) * mm, "end": v(218.18, 57.3) * mm, "construction": true});
            skLineSegment(sketch, "E941.MirrorCS", {"start": v(142.16, 46.76) * mm, "end": v(179.74, 47.21) * mm});
            skLineSegment(sketch, "E942.MirrorCS", {"start": v(436.55, 42.67) * mm, "end": v(457.6, 42.82) * mm});
            skLineSegment(sketch, "E943.MirrorCS", {"start": v(257.68, 56.43) * mm, "end": v(288.78, 56.95) * mm});
            skLineSegment(sketch, "E944.MirrorCS", {"start": v(354.83, 50.84) * mm, "end": v(380.47, 51.14) * mm});
            skLineSegment(sketch, "E945.MirrorCS", {"start": v(291.98, 40.1) * mm, "end": v(321.15, 40.32) * mm});
            skLineSegment(sketch, "E946.MirrorCS", {"start": v(436.56, 41.15) * mm, "end": v(457.62, 41.3) * mm});
            skLineSegment(sketch, "E947.MirrorCS", {"start": v(182.9, 40.85) * mm, "end": v(218.2, 41.1) * mm});
            skLineSegment(sketch, "E948.MirrorCS", {"start": v(221.35, 57.34) * mm, "end": v(254.48, 57.9) * mm});
            skLineSegment(sketch, "E949.MirrorCS", {"start": v(525.63, 41.79) * mm, "end": v(541.7, 41.9) * mm});
            skLineSegment(sketch, "E950.MirrorCS", {"start": v(436.52, 51.82) * mm, "end": v(457.58, 52.07) * mm});
            skLineSegment(sketch, "E951.MirrorCS", {"start": v(98.97, 40.24) * mm, "end": v(138.98, 40.53) * mm});
            skLineSegment(sketch, "E952.MirrorCS", {"start": v(544.87, 41.93) * mm, "end": v(559.85, 42.04) * mm});
            skLineSegment(sketch, "E953.MirrorCS", {"start": v(4.75, 46.63) * mm, "end": v(50.05, 47.18) * mm});
            skLineSegment(sketch, "E954.MirrorCS", {"start": v(-33.04, 56.39) * mm, "end": v(118.54, 56.39) * mm, "construction": true});
            skLineSegment(sketch, "E955.MirrorCS", {"start": v(525.56, 62.46) * mm, "end": v(541.61, 62.73) * mm});
            skLineSegment(sketch, "E956.MirrorCS", {"start": v(291.95, 57) * mm, "end": v(321.12, 57.5) * mm});
            skLineSegment(sketch, "E957.MirrorCS", {"start": v(436.51, 59.44) * mm, "end": v(457.57, 59.79) * mm});
            skLineSegment(sketch, "E958.MirrorCS", {"start": v(53.23, 32.6) * mm, "end": v(95.8, 32.71) * mm});
            skLineSegment(sketch, "E959.MirrorCS", {"start": v(483.67, 32.12) * mm, "end": v(502.09, 32.16) * mm});
            skLineSegment(sketch, "E960.MirrorCS", {"start": v(324.31, 41.86) * mm, "end": v(351.67, 42.06) * mm});
            skLineSegment(sketch, "E961.MirrorCS", {"start": v(53.22, 47.22) * mm, "end": v(95.8, 47.73) * mm});
            skLineSegment(sketch, "E962.MirrorCS", {"start": v(53.24, 38.39) * mm, "end": v(95.81, 38.7) * mm});
            skLineSegment(sketch, "E963.MirrorCS", {"start": v(544.83, 53.12) * mm, "end": v(559.8, 53.3) * mm});
            skLineSegment(sketch, "E964.MirrorCS", {"start": v(483.65, 50.86) * mm, "end": v(502.06, 51.08) * mm});
            skLineSegment(sketch, "E965.MirrorCS", {"start": v(544.81, 61.26) * mm, "end": v(559.8, 61.5) * mm});
            skLineSegment(sketch, "E966.MirrorCS", {"start": v(4.77, 38.04) * mm, "end": v(50.06, 38.37) * mm});
            skLineSegment(sketch, "E967.MirrorCS", {"start": v(291.95, 50.08) * mm, "end": v(321.12, 50.43) * mm});
            skLineSegment(sketch, "E968.MirrorCS", {"start": v(324.31, 48.95) * mm, "end": v(351.67, 49.27) * mm});
            skLineSegment(sketch, "E969.MirrorCS", {"start": v(460.77, 50.58) * mm, "end": v(480.47, 50.82) * mm});
            skLineSegment(sketch, "E970.MirrorCS", {"start": v(525.58, 60.93) * mm, "end": v(541.64, 61.2) * mm});
            skLineSegment(sketch, "E971.MirrorCS", {"start": v(291.98, 33.18) * mm, "end": v(321.15, 33.25) * mm});
            skLineSegment(sketch, "E972.MirrorCS", {"start": v(505.25, 43.17) * mm, "end": v(522.45, 43.3) * mm});
            skLineSegment(sketch, "E973.MirrorCS", {"start": v(410.87, 42.49) * mm, "end": v(433.37, 42.65) * mm});
            skLineSegment(sketch, "E974.MirrorCS", {"start": v(383.65, 51.18) * mm, "end": v(407.67, 51.47) * mm});
            skLineSegment(sketch, "E975.MirrorCS", {"start": v(505.18, 62.11) * mm, "end": v(522.38, 62.4) * mm});
            skLineSegment(sketch, "E976.MirrorCS", {"start": v(383.68, 33.4) * mm, "end": v(407.7, 33.46) * mm});
            skLineSegment(sketch, "E977.MirrorCS", {"start": v(483.65, 43.01) * mm, "end": v(502.07, 43.14) * mm});
            skLineSegment(sketch, "E978.MirrorCS", {"start": v(221.4, 39.6) * mm, "end": v(254.53, 39.84) * mm});
            skLineSegment(sketch, "E979.MirrorCS", {"start": v(383.68, 40.77) * mm, "end": v(407.7, 40.94) * mm});
            skLineSegment(sketch, "E980.MirrorCS", {"start": v(98.98, 46.24) * mm, "end": v(138.99, 46.72) * mm});
            skLineSegment(sketch, "E981.MirrorCS", {"start": v(221.38, 55.82) * mm, "end": v(254.5, 56.38) * mm});
            skLineSegment(sketch, "E982.MirrorCS", {"start": v(525.6, 52.88) * mm, "end": v(541.65, 53.08) * mm});
            skLineSegment(sketch, "E983.MirrorCS", {"start": v(257.7, 41.38) * mm, "end": v(288.8, 41.6) * mm});
            skLineSegment(sketch, "E984.MirrorCS", {"start": v(505.26, 41.64) * mm, "end": v(522.46, 41.77) * mm});
            skLineSegment(sketch, "E985.MirrorCS", {"start": v(221.37, 49.23) * mm, "end": v(254.5, 49.63) * mm});
            skLineSegment(sketch, "E986.MirrorCS", {"start": v(257.66, 57.95) * mm, "end": v(288.75, 58.48) * mm});
            skLineSegment(sketch, "E987.MirrorCS", {"start": v(505.2, 60.6) * mm, "end": v(522.4, 60.88) * mm});
            skLineSegment(sketch, "E988.MirrorCS", {"start": v(0, 38.77) * mm, "end": v(648.23, 43.43) * mm, "construction": true});
            skLineSegment(sketch, "E989.MirrorCS", {"start": v(354.85, 42.08) * mm, "end": v(380.5, 42.27) * mm});
            skLineSegment(sketch, "E990.MirrorCS", {"start": v(98.98, 32.72) * mm, "end": v(138.99, 32.81) * mm});
            skLineSegment(sketch, "E991.MirrorCS", {"start": v(98.97, 47.76) * mm, "end": v(138.97, 48.25) * mm});
            skLineSegment(sketch, "E992.MirrorCS", {"start": v(354.8, 59.59) * mm, "end": v(380.44, 60.02) * mm});
            skLineSegment(sketch, "E993.MirrorCS", {"start": v(53.23, 31.08) * mm, "end": v(95.8, 31.19) * mm});
            skLineSegment(sketch, "E994.MirrorCS", {"start": v(460.8, 32.82) * mm, "end": v(460.8, 33.59) * mm});
            skLineSegment(sketch, "E995.MirrorCS", {"start": v(433.38, 33.52) * mm, "end": v(433.39, 32.76) * mm});
            skLineSegment(sketch, "E996.MirrorCS", {"start": v(142.13, 56.01) * mm, "end": v(179.7, 56.65) * mm});
            skLineSegment(sketch, "E997.MirrorCS", {"start": v(436.56, 32.77) * mm, "end": v(436.56, 33.53) * mm});
            skLineSegment(sketch, "E998.MirrorCS", {"start": v(354.86, 33.33) * mm, "end": v(380.5, 33.4) * mm});
            skLineSegment(sketch, "E999.MirrorCS", {"start": v(383.62, 60.07) * mm, "end": v(407.64, 60.47) * mm});
            skLineSegment(sketch, "E1000.MirrorCS", {"start": v(0, 45.05) * mm, "end": v(642.94, 52.77) * mm, "construction": true});
            skLineSegment(sketch, "E1001.MirrorCS", {"start": v(98.99, 38.72) * mm, "end": v(139, 39) * mm});
            skLineSegment(sketch, "E1002.MirrorCS", {"start": v(257.7, 33.1) * mm, "end": v(288.8, 33.17) * mm});
            skLineSegment(sketch, "E1003.MirrorCS", {"start": v(480.5, 33.63) * mm, "end": v(480.5, 32.87) * mm});
            skLineSegment(sketch, "E1004.MirrorCS", {"start": v(460.75, 59.84) * mm, "end": v(480.44, 60.17) * mm});
            skLineSegment(sketch, "E1005.MirrorCS", {"start": v(221.4, 31.49) * mm, "end": v(254.53, 31.57) * mm});
            skLineSegment(sketch, "E1006.MirrorCS", {"start": v(483.67, 33.64) * mm, "end": v(502.09, 33.69) * mm});
            skLineSegment(sketch, "E1007.MirrorCS", {"start": v(436.49, 60.96) * mm, "end": v(457.55, 61.31) * mm});
            skLineSegment(sketch, "E1008.MirrorCS", {"start": v(4.76, 30.97) * mm, "end": v(50.06, 31.08) * mm});
            skLineSegment(sketch, "E1009.MirrorCS", {"start": v(410.88, 33.47) * mm, "end": v(433.38, 33.52) * mm});
            skLineSegment(sketch, "E1010.MirrorCS", {"start": v(0, 52.1) * mm, "end": v(642.9, 62.9) * mm, "construction": true});
            skLineSegment(sketch, "E1011.MirrorCS", {"start": v(98.98, 53.76) * mm, "end": v(138.98, 54.44) * mm});
            skLineSegment(sketch, "E1012.MirrorCS", {"start": v(460.72, 61.37) * mm, "end": v(480.42, 61.7) * mm});
            skLineSegment(sketch, "E1013.MirrorCS", {"start": v(410.84, 59) * mm, "end": v(433.34, 59.38) * mm});
            skLineSegment(sketch, "E1014.MirrorCS", {"start": v(142.16, 32.82) * mm, "end": v(179.74, 32.91) * mm});
            skLineSegment(sketch, "E1015.MirrorCS", {"start": v(182.92, 31.4) * mm, "end": v(218.22, 31.48) * mm});
            skLineSegment(sketch, "E1016.MirrorCS", {"start": v(0, 45.82) * mm, "end": v(648.2, 53.6) * mm, "construction": true});
            skLineSegment(sketch, "E1017.MirrorCS", {"start": v(4.76, 32.5) * mm, "end": v(50.06, 32.6) * mm});
            skLineSegment(sketch, "E1018.MirrorCS", {"start": v(544.87, 33.79) * mm, "end": v(559.86, 33.82) * mm});
            skLineSegment(sketch, "E1019.MirrorCS", {"start": v(98.96, 55.29) * mm, "end": v(138.96, 55.96) * mm});
            skLineSegment(sketch, "E1020.MirrorCS", {"start": v(436.56, 33.53) * mm, "end": v(457.62, 33.58) * mm});
            skLineSegment(sketch, "E1021.MirrorCS", {"start": v(142.17, 31.3) * mm, "end": v(179.74, 31.39) * mm});
            skLineSegment(sketch, "E1022.MirrorCS", {"start": v(182.88, 56.7) * mm, "end": v(218.18, 57.3) * mm});
            skLineSegment(sketch, "E1023.MirrorCS", {"start": v(460.8, 32.06) * mm, "end": v(480.5, 32.1) * mm});
            skLineSegment(sketch, "E1024.MirrorCS", {"start": v(410.82, 60.53) * mm, "end": v(433.31, 60.9) * mm});
            skLineSegment(sketch, "E1025.MirrorCS", {"start": v(483.6, 61.75) * mm, "end": v(502, 62.06) * mm});
            skLineSegment(sketch, "E1026.MirrorCS", {"start": v(383.64, 58.55) * mm, "end": v(407.67, 58.95) * mm});
            skLineSegment(sketch, "E1027.MirrorCS", {"start": v(221.4, 33.01) * mm, "end": v(254.53, 33.1) * mm});
            skLineSegment(sketch, "E1028.MirrorCS", {"start": v(98.98, 31.2) * mm, "end": v(139, 31.29) * mm});
            skLineSegment(sketch, "E1029.MirrorCS", {"start": v(0, 38) * mm, "end": v(642.97, 42.63) * mm, "construction": true});
            skLineSegment(sketch, "E1030.MirrorCS", {"start": v(525.64, 33.74) * mm, "end": v(541.7, 33.78) * mm});
            skLineSegment(sketch, "E1031.MirrorCS", {"start": v(457.62, 33.58) * mm, "end": v(457.62, 32.82) * mm});
            skLineSegment(sketch, "E1032.MirrorCS", {"start": v(324.33, 31.73) * mm, "end": v(351.69, 31.8) * mm});
            skLineSegment(sketch, "E1033.MirrorCS", {"start": v(354.86, 31.8) * mm, "end": v(380.5, 31.87) * mm});
            skLineSegment(sketch, "E1034.MirrorCS", {"start": v(383.68, 32.64) * mm, "end": v(383.68, 31.88) * mm});
            skLineSegment(sketch, "E1035.MirrorCS", {"start": v(383.68, 31.88) * mm, "end": v(407.71, 31.93) * mm});
            skLineSegment(sketch, "E1036.MirrorCS", {"start": v(407.71, 31.93) * mm, "end": v(407.7, 32.7) * mm});
            skLineSegment(sketch, "E1037.MirrorCS", {"start": v(0, 30.96) * mm, "end": v(642.98, 32.5) * mm, "construction": true});
            skLineSegment(sketch, "E1038.MirrorCS", {"start": v(410.89, 31.94) * mm, "end": v(433.39, 32) * mm});
            skLineSegment(sketch, "E1039.MirrorCS", {"start": v(433.39, 32) * mm, "end": v(433.39, 32.76) * mm});
            skLineSegment(sketch, "E1040.MirrorCS", {"start": v(410.88, 32.7) * mm, "end": v(410.89, 31.94) * mm});
            skLineSegment(sketch, "E1041.MirrorCS", {"start": v(436.56, 32) * mm, "end": v(457.62, 32.05) * mm});
            skLineSegment(sketch, "E1042.MirrorCS", {"start": v(436.56, 32.77) * mm, "end": v(436.56, 32) * mm});
            skLineSegment(sketch, "E1043.MirrorCS", {"start": v(457.62, 32.05) * mm, "end": v(457.62, 32.82) * mm});
            skLineSegment(sketch, "E1044.MirrorCS", {"start": v(505.26, 32.17) * mm, "end": v(522.47, 32.21) * mm});
            skLineSegment(sketch, "E1045.MirrorCS", {"start": v(483.67, 32.88) * mm, "end": v(483.67, 32.12) * mm});
            skLineSegment(sketch, "E1046.MirrorCS", {"start": v(502.09, 32.16) * mm, "end": v(502.09, 32.92) * mm});
            skLineSegment(sketch, "E1047.MirrorCS", {"start": v(502.09, 33.69) * mm, "end": v(502.09, 32.92) * mm});
            skLineSegment(sketch, "E1048.MirrorCS", {"start": v(460.8, 32.82) * mm, "end": v(460.8, 32.06) * mm});
            skLineSegment(sketch, "E1049.MirrorCS", {"start": v(480.5, 32.1) * mm, "end": v(480.5, 32.87) * mm});
            skLineSegment(sketch, "E1050.MirrorCS", {"start": v(483.67, 32.88) * mm, "end": v(483.67, 33.64) * mm});
            skLineSegment(sketch, "E1051.MirrorCS", {"start": v(522.46, 33.73) * mm, "end": v(522.47, 32.97) * mm});
            skLineSegment(sketch, "E1052.MirrorCS", {"start": v(505.26, 32.93) * mm, "end": v(505.26, 33.7) * mm});
            skLineSegment(sketch, "E1053.MirrorCS", {"start": v(0, 31.72) * mm, "end": v(648.25, 33.27) * mm, "construction": true});
            skLineSegment(sketch, "E1054.MirrorCS", {"start": v(505.26, 32.93) * mm, "end": v(505.26, 32.17) * mm});
            skLineSegment(sketch, "E1055.MirrorCS", {"start": v(522.47, 32.21) * mm, "end": v(522.47, 32.97) * mm});
            skLineSegment(sketch, "E1056.MirrorCS", {"start": v(525.64, 32.98) * mm, "end": v(525.64, 32.22) * mm});
            skLineSegment(sketch, "E1057.MirrorCS", {"start": v(525.64, 32.98) * mm, "end": v(525.64, 33.74) * mm});
            skLineSegment(sketch, "E1058.MirrorCS", {"start": v(541.7, 32.26) * mm, "end": v(541.7, 33.02) * mm});
            skLineSegment(sketch, "E1059.MirrorCS", {"start": v(541.7, 33.78) * mm, "end": v(541.7, 33.02) * mm});
            skLineSegment(sketch, "E1060.MirrorCS", {"start": v(525.64, 32.22) * mm, "end": v(541.7, 32.26) * mm});
            skLineSegment(sketch, "E1061.MirrorCS", {"start": v(544.88, 33.03) * mm, "end": v(544.88, 32.26) * mm});
            skLineSegment(sketch, "E1062.MirrorCS", {"start": v(544.88, 32.26) * mm, "end": v(559.86, 32.3) * mm});
            skLineSegment(sketch, "E1063.MirrorCS", {"start": v(559.86, 32.3) * mm, "end": v(559.86, 33.06) * mm});
            skLineSegment(sketch, "E1064.MirrorCS", {"start": v(559.86, 33.82) * mm, "end": v(559.86, 33.06) * mm});
            skLineSegment(sketch, "E1065.MirrorCS", {"start": v(544.88, 33.03) * mm, "end": v(544.87, 33.79) * mm});
            skLineSegment(sketch, "E1066.MirrorCS", {"start": v(622.85, 32.45) * mm, "end": v(622.85, 33.21) * mm});
            skLineSegment(sketch, "E1067.MirrorCS", {"start": v(608.43, 33.94) * mm, "end": v(608.44, 33.18) * mm});
            skLineSegment(sketch, "E1068.MirrorCS", {"start": v(563.03, 33.07) * mm, "end": v(563.03, 33.83) * mm});
            skLineSegment(sketch, "E1069.MirrorCS", {"start": v(563.03, 33.07) * mm, "end": v(563.03, 32.3) * mm});
            skLineSegment(sketch, "E1070.MirrorCS", {"start": v(577, 32.34) * mm, "end": v(577, 33.1) * mm});
            skLineSegment(sketch, "E1071.MirrorCS", {"start": v(580.17, 33.11) * mm, "end": v(580.17, 32.35) * mm});
            skLineSegment(sketch, "E1072.MirrorCS", {"start": v(611.61, 33.19) * mm, "end": v(611.6, 33.95) * mm});
            skLineSegment(sketch, "E1073.MirrorCS", {"start": v(593.17, 32.38) * mm, "end": v(593.17, 33.14) * mm});
            skLineSegment(sketch, "E1074.MirrorCS", {"start": v(596.34, 33.15) * mm, "end": v(596.34, 33.91) * mm});
            skLineSegment(sketch, "E1075.MirrorCS", {"start": v(596.34, 33.15) * mm, "end": v(596.35, 32.39) * mm});
            skLineSegment(sketch, "E1076.MirrorCS", {"start": v(577, 33.86) * mm, "end": v(577, 33.1) * mm});
            skLineSegment(sketch, "E1077.MirrorCS", {"start": v(580.17, 33.11) * mm, "end": v(580.17, 33.87) * mm});
            skLineSegment(sketch, "E1078.MirrorCS", {"start": v(608.44, 32.42) * mm, "end": v(608.44, 33.18) * mm});
            skLineSegment(sketch, "E1079.MirrorCS", {"start": v(622.84, 33.98) * mm, "end": v(622.85, 33.21) * mm});
            skLineSegment(sketch, "E1080.MirrorCS", {"start": v(611.61, 33.19) * mm, "end": v(611.61, 32.42) * mm});
            skLineSegment(sketch, "E1081.MirrorCS", {"start": v(593.17, 33.9) * mm, "end": v(593.17, 33.14) * mm});
            skLineSegment(sketch, "E1082.MirrorCS", {"start": v(580.17, 33.87) * mm, "end": v(593.17, 33.9) * mm});
            skLineSegment(sketch, "E1083.MirrorCS", {"start": v(563.03, 33.83) * mm, "end": v(577, 33.86) * mm});
            skLineSegment(sketch, "E1084.MirrorCS", {"start": v(563.03, 32.3) * mm, "end": v(577, 32.34) * mm});
            skLineSegment(sketch, "E1085.MirrorCS", {"start": v(611.6, 33.95) * mm, "end": v(622.84, 33.98) * mm});
            skLineSegment(sketch, "E1086.MirrorCS", {"start": v(596.34, 33.91) * mm, "end": v(608.43, 33.94) * mm});
            skLineSegment(sketch, "E1087.MirrorCS", {"start": v(580.17, 32.35) * mm, "end": v(593.17, 32.38) * mm});
            skLineSegment(sketch, "E1088.MirrorCS", {"start": v(596.35, 32.39) * mm, "end": v(608.44, 32.42) * mm});
            skLineSegment(sketch, "E1089.MirrorCS", {"start": v(611.61, 32.42) * mm, "end": v(622.85, 32.45) * mm});
            skLineSegment(sketch, "E1090.MirrorCS", {"start": v(380.5, 31.87) * mm, "end": v(380.5, 32.63) * mm});
            skSolve(sketch);
        }
        {
            var Q0;
            Q0=qCreatedBy(makeId("Front.planeOp"),FACE);
            var sketch = newSketch(context, id + "F1", { "sketchPlane" : qUnion([Q0])});
            skLineSegment(sketch, "E1091", {"start": v(0, 0) * mm, "end": v(0, 56.39) * mm});
            skLineSegment(sketch, "E1092", {"start": v(0, 56.39) * mm, "end": v(635, 68.83) * mm});
            skLineSegment(sketch, "E1093", {"start": v(635, 68.83) * mm, "end": v(635, -12.45) * mm});
            skLineSegment(sketch, "E1094", {"start": v(635, -12.45) * mm, "end": v(0, 0) * mm});
            skLineSegment(sketch, "E1095", {"start": v(0, 28.2) * mm, "end": v(897.35, 28.2) * mm, "construction": true});
            skSolve(sketch);
        }
        {
            var Q0;
            Q0=qSketchRegion(id+"F1",true);
            extrude(context, id + "F2", {"entities" : qUnion([Q0]), "depth" : 4.76 * mm});
        }
        {
            var Q0;
            Q0=makeQuery(id+"F2.opExtrude","CAP_FACE",FACE,{"disambiguationData":[OSD([sQuery(id+"F1.wireOp",EDGE,"E1091"),sQuery(id+"F1.wireOp",EDGE,"E1092"),sQuery(id+"F1.wireOp",EDGE,"E1093"),sQuery(id+"F1.wireOp",EDGE,"E1094")])],"isStart":false});
            var sketch = newSketch(context, id + "F3", { "sketchPlane" : qUnion([Q0])});
            skLineSegment(sketch, "E1096", {"start": v(0, 28.2) * mm, "end": v(635, 28.2) * mm, "construction": true});
            skSolve(sketch);
        }
        {
            var Q0;
            Q0=qSketchRegion(id+"F0",true);
            extrude(context, id + "F4", {"entities" : qUnion([Q0]), "operationType" : NewBodyOperationType.REMOVE, "endBound" : BoundingType.THROUGH_ALL, "depth" : 25.4 * mm});
        }
        {
            var Q0;
            Q0=makeQuery(id+"F3.imprint","IMPRINT",FACE,{"disambiguationData":[TD([[makeQuery(id+"F3.imprint","IMPRINT",EDGE,{"derivedFrom":makeQuery(id+"F2.opExtrude","CAP_EDGE",EDGE,{"disambiguationData":[OSD([sQuery(id+"F1.wireOp",EDGE,"E1091")])],"isStart":false})}),-1.0]])]});
            var sketch = newSketch(context, id + "F5", { "sketchPlane" : qUnion([Q0])});
            skCircle(sketch, "E1097", {"center": v(97.4, 13.14) * mm, "radius": 1.13 * mm});
            skLineSegment(sketch, "E1098", {"start": v(0, 14.1) * mm, "end": v(635, 7.87) * mm, "construction": true});
            skCircle(sketch, "E1099", {"center": v(3.18, 14.07) * mm, "radius": 1.13 * mm});
            skCircle(sketch, "E1100", {"center": v(181.33, 12.32) * mm, "radius": 1.13 * mm});
            skCircle(sketch, "E1101", {"center": v(290.4, 11.25) * mm, "radius": 1.13 * mm});
            skCircle(sketch, "E1102", {"center": v(409.3, 10.09) * mm, "radius": 1.13 * mm});
            skCircle(sketch, "E1103", {"center": v(524.06, 8.96) * mm, "radius": 1.13 * mm});
            skCircle(sketch, "E1104", {"center": v(624.44, 7.98) * mm, "radius": 1.13 * mm});
            skCircle(sketch, "E1105.MirrorC", {"center": v(97.4, 43.25) * mm, "radius": 1.13 * mm});
            skCircle(sketch, "E1106.MirrorC", {"center": v(3.18, 42.32) * mm, "radius": 1.13 * mm});
            skCircle(sketch, "E1107.MirrorC", {"center": v(181.33, 44.07) * mm, "radius": 1.13 * mm});
            skCircle(sketch, "E1108.MirrorC", {"center": v(290.4, 45.14) * mm, "radius": 1.13 * mm});
            skCircle(sketch, "E1109.MirrorC", {"center": v(409.3, 46.3) * mm, "radius": 1.13 * mm});
            skCircle(sketch, "E1110.MirrorC", {"center": v(524.06, 47.43) * mm, "radius": 1.13 * mm});
            skCircle(sketch, "E1111.MirrorC", {"center": v(624.44, 48.41) * mm, "radius": 1.13 * mm});
            skSolve(sketch);
        }
        {
            var Q0;
            Q0=qSketchRegion(id+"F5",true);
            extrude(context, id + "F6", {"entities" : qUnion([Q0]), "operationType" : NewBodyOperationType.REMOVE, "endBound" : BoundingType.THROUGH_ALL, "depth" : 25.4 * mm});
        }
        {
            assignVariable(context, id + "F7", {"name" : "swheight", "anyValue" : 1 * mm});
        }
        {
            var Q0;
            Q0=qSketchRegion(id+"F5",true);
            extrude(context, id + "F8", {"entities" : qUnion([Q0]), "operationType" : NewBodyOperationType.REMOVE, "endBound" : BoundingType.THROUGH_ALL, "oppositeDirection" : true, "depth" : 25.4 * mm});
        }
        {
            var Q0;
            Q0=makeQuery(id+"F2.opExtrude","CAP_FACE",FACE,{"disambiguationData":[OSD([sQuery(id+"F1.wireOp",EDGE,"E1091"),sQuery(id+"F1.wireOp",EDGE,"E1092"),sQuery(id+"F1.wireOp",EDGE,"E1093"),sQuery(id+"F1.wireOp",EDGE,"E1094")])],"isStart":false});
            var sketch = newSketch(context, id + "F9", { "sketchPlane" : qUnion([Q0])});
            skLineSegment(sketch, "E1112.bottom", {"start": v(7.86, 6.59) * mm, "end": v(14.36, 6.59) * mm});
            skLineSegment(sketch, "E1112.top", {"start": v(7.86, 0.09) * mm, "end": v(14.36, 0.09) * mm});
            skLineSegment(sketch, "E1112.left", {"start": v(7.86, 6.59) * mm, "end": v(7.86, 0.09) * mm});
            skLineSegment(sketch, "E1112.right", {"start": v(14.36, 6.59) * mm, "end": v(14.36, 0.09) * mm});
            skPoint(sketch, "E1112.middle", {"position": v(11.11, 3.34) * mm});
            skLineSegment(sketch, "E1113.bottom", {"start": v(7.86, 13.69) * mm, "end": v(14.36, 13.69) * mm});
            skLineSegment(sketch, "E1113.top", {"start": v(7.86, 7.19) * mm, "end": v(14.36, 7.19) * mm});
            skLineSegment(sketch, "E1113.left", {"start": v(7.86, 13.69) * mm, "end": v(7.86, 7.19) * mm});
            skLineSegment(sketch, "E1113.right", {"start": v(14.36, 13.69) * mm, "end": v(14.36, 7.19) * mm});
            skPoint(sketch, "E1113.middle", {"position": v(11.11, 10.44) * mm});
            skPoint(sketch, "E1113.middle.positionSnap0", {"position": v(11.11, 6.59) * mm});
            skPoint(sketch, "E1113.centerSnap0", {"position": v(11.11, 6.59) * mm});
            skLineSegment(sketch, "E1114", {"start": v(4.77, 3.44) * mm, "end": v(622.77, -6.94) * mm, "construction": true});
            skPoint(sketch, "E1114.startSnap0", {"position": v(4.76, 3.44) * mm});
            skPoint(sketch, "E1114.endSnap0", {"position": v(622.76, -6.94) * mm});
            skLineSegment(sketch, "E1115.bottom", {"start": v(40.46, 6.04) * mm, "end": v(46.96, 6.04) * mm});
            skLineSegment(sketch, "E1115.top", {"start": v(40.46, -0.46) * mm, "end": v(46.96, -0.46) * mm});
            skLineSegment(sketch, "E1115.left", {"start": v(40.46, 6.04) * mm, "end": v(40.46, -0.46) * mm});
            skLineSegment(sketch, "E1115.right", {"start": v(46.96, 6.04) * mm, "end": v(46.96, -0.46) * mm});
            skPoint(sketch, "E1115.middle", {"position": v(43.7, 2.8) * mm});
            skSolve(sketch);
        }
        {
            var Q0;
            Q0 = qSketchRegion(id + "F9", true);
            extrude(context, id + "F10", {"entities" : qUnion([Q0]), "operationType" : NewBodyOperationType.REMOVE, "oppositeDirection" : true, "depth" : getVariable(context, 'swheight')});
        }
    });
